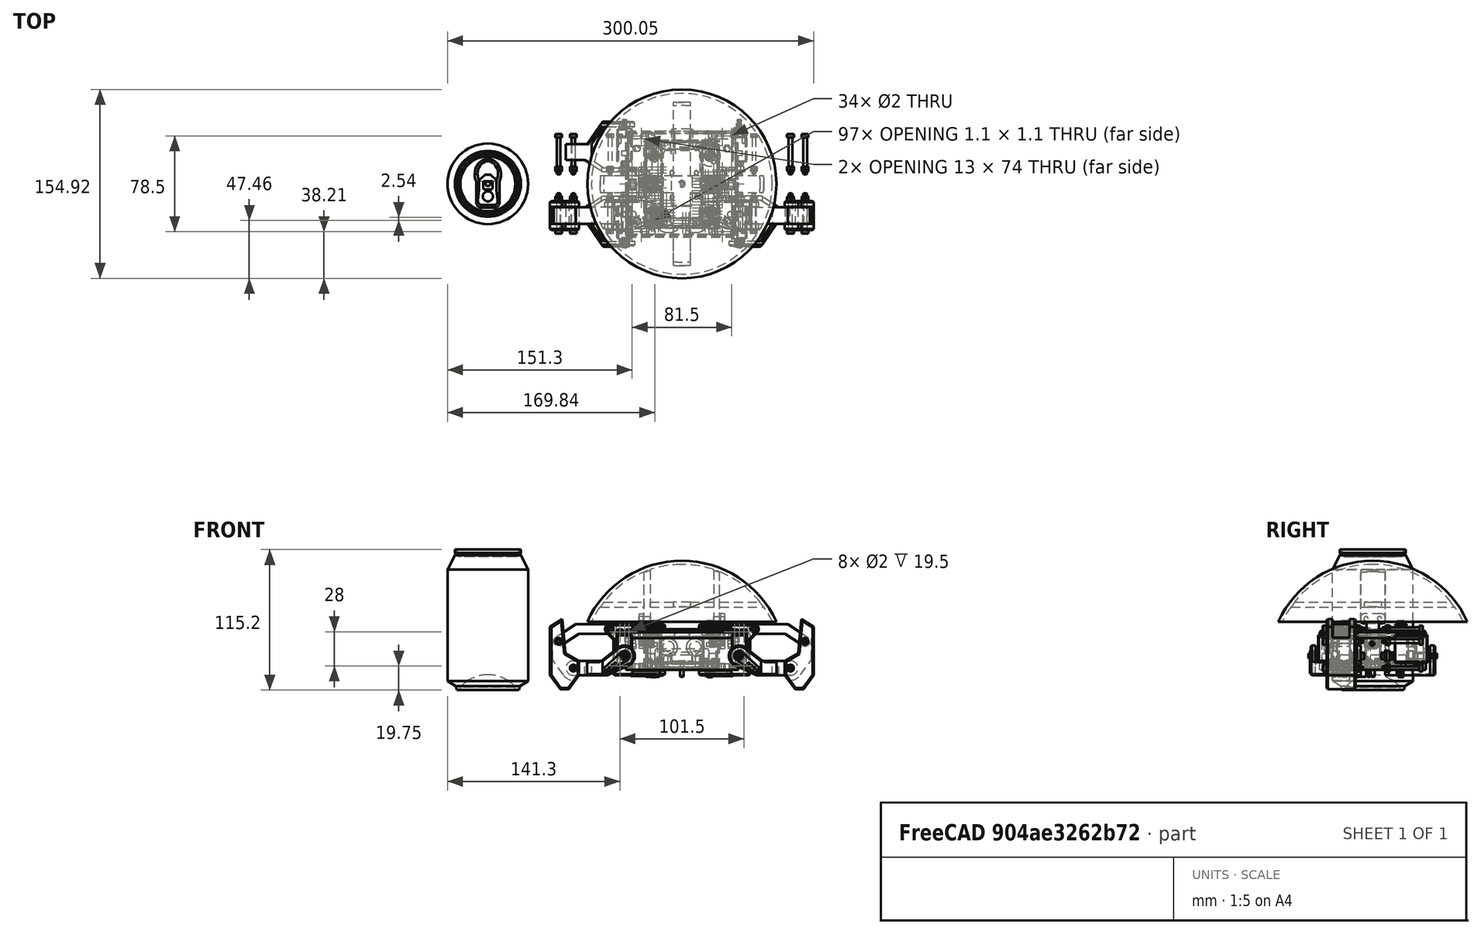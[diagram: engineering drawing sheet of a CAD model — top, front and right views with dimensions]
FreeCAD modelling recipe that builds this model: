
FCSTD DOCUMENT  (FreeCAD 0.16R6692 (Git))
Label: icezumKame
License: All rights reserved
LicenseURL: http://es.wikipedia.org/wiki/Todos_los_derechos_reservados
objects: Part::FeaturePython×116, Part::Cut×39, Part::MultiFuse×32, Sketcher::SketchObject×30, PartDesign::Pad×30, Part::Mirroring×30, Part::Feature×25, Part::Cylinder×23, Part::Box×19, App::DocumentObjectGroup×14, Part::Fillet×10, Part::Chamfer×10, Part::Prism×8, Part::MultiCommon×2, Part::Cone×2, Part::Sphere×2, Spreadsheet::Sheet×1, Mesh::Feature×1
note: 408 computed .brp shape members not serialized (recipe doc carries the construction recipe); baked Part::Feature solids carry a one-line shape summary decoded from their .brp

FEATURE [Part::Feature] Solid001  label="TGY-306G"
  shape: bbox 12.2 x 32 x 31.85 mm, 251 faces (baked)
FEATURE [Part::Box] Box  label="Cubo"
  Height = 10
  Length = 30
  Width = 55
FEATURE [Part::Fillet] Fillet  label="battery"
  Base = -> Box
  Edges = 12 edges r=2.5: [Edge1,Edge2,Edge3,Edge4,Edge5,Edge6,Edge7,Edge8,Edge9,Edge10,Edge11,Edge12]
FEATURE [Part::FeaturePython] Clone002  label="Clone of battery"  # Draft clone (typed FeaturePython)
  Objects = -> [Fillet]
  Placement = pos=(-15,-27.5,-2) rot=(0,0,1;0rad)
  Scale = (1,1,1)
FEATURE [Part::FeaturePython] Clone005  label="Clone of TGY-306G003"  # Draft clone (typed FeaturePython)
  Objects = -> [Solid001]
  Placement = pos=(-23,23,23.3) rot=(0,1,0;3.14159rad)
  Scale = (1,1,1)
FEATURE [Part::Box] Box001  label="main_cube"
  Height = 26
  Length = 92
  Placement = pos=(-46,-43,-3.5) rot=(0,0,1;0rad)
  Width = 87
FEATURE [Part::Feature] Part__Feature  label="final-can"
  Placement = pos=(-159,0,-21) rot=(0,0,1;0rad)
  shape: bbox 66.1 x 66.1 x 115.2 mm, 53 faces (baked)
FEATURE [Sketcher::SketchObject] Sketch  label="servo_sketch"
  Placement = pos=(0,0,-10) rot=(1,0,0;3.14159rad)
  sketch-geometry (14):
    g0: LineSegment StartX=-29.5 StartY=29 StartZ=0 EndX=-16.5 EndY=29 EndZ=0
    g1: LineSegment StartX=-16.5 StartY=29 StartZ=0 EndX=-16.5 EndY=5.5 EndZ=0
    g2: LineSegment StartX=-16.5 StartY=5.5 StartZ=0 EndX=-29.5 EndY=5.5 EndZ=0
    g3: LineSegment StartX=-29.5 StartY=5.5 StartZ=0 EndX=-29.5 EndY=29 EndZ=0
    g4: Circle CenterX=-26.75 CenterY=31.25 CenterZ=0 NormalX=0 NormalY=0 NormalZ=1 Radius=1
    g5: Circle CenterX=-19.25 CenterY=31.25 CenterZ=0 NormalX=0 NormalY=0 NormalZ=1 Radius=1
    g6: Circle CenterX=-26.75 CenterY=3.25 CenterZ=0 NormalX=0 NormalY=0 NormalZ=1 Radius=1
    g7: Circle CenterX=-19.25 CenterY=3.25 CenterZ=0 NormalX=0 NormalY=0 NormalZ=1 Radius=1
    g8: LineSegment [constr] StartX=-29.5 StartY=29 StartZ=0 EndX=-26.75 EndY=31.25 EndZ=0
    g9: LineSegment [constr] StartX=-26.75 StartY=31.25 StartZ=0 EndX=-19.25 EndY=31.25 EndZ=0
    g10: LineSegment [constr] StartX=-19.25 StartY=31.25 StartZ=0 EndX=-16.5 EndY=29 EndZ=0
    g11: LineSegment [constr] StartX=-29.5 StartY=5.5 StartZ=0 EndX=-26.75 EndY=3.25 EndZ=0
    g12: LineSegment [constr] StartX=-26.75 StartY=3.25 StartZ=0 EndX=-19.25 EndY=3.25 EndZ=0
    g13: LineSegment [constr] StartX=-19.25 StartY=3.25 StartZ=0 EndX=-16.5 EndY=5.5 EndZ=0
  constraints (33):
    c: Coincident(g0,g1)
    c: Coincident(g1,g2)
    c: Coincident(g2,g3)
    c: Coincident(g3,g0)
    c: Horizontal(g0)
    c: Horizontal(g2)
    c: Vertical(g1)
    c: Vertical(g3)
    c: Coincident(g0,g8)
    c: Coincident(g8,g4)
    c: Coincident(g8,g9)
    c: Coincident(g9,g5)
    c: Horizontal(g9)
    c: Coincident(g9,g10)
    c: Coincident(g10,g0)
    c: Coincident(g2,g11)
    c: Coincident(g11,g6)
    c: Coincident(g11,g12)
    c: Coincident(g12,g7)
    c: Horizontal(g12)
    c: Coincident(g12,g13)
    c: Coincident(g13,g1)
    c: Radius(g4) = 1
    c: Equal(g4,g5)
    c: Equal(g4,g6)
    c: Equal(g4,g7)
    c: Equal(g8,g10)
    c: Equal(g11,g13)
    c: Distance(g3) = 23.5
    c: Distance(g2) = 13
    c: DistanceY(g-1,g1) = 5.5
    c: DistanceX(g-1,g1) = -16.5
    c: DistanceY(g7,g1) = 2.25
FEATURE [PartDesign::Pad] Pad  label="original_servo_hole"
  Length = 40
  Length2 = 100
  Placement = pos=(0,0,-10) rot=(1,0,0;3.14159rad)
  Reversed = true
  Sketch = -> Sketch
  Type = 0
FEATURE [Part::Box] Box007  label="difference_cube"
  Height = 27
  Length = 88
  Placement = pos=(-44,-41,1.5) rot=(0,0,1;0rad)
  Width = 83
FEATURE [Part::Box] Box008  label="difference_cube_board_bed"
  Height = 27
  Length = 58
  Placement = pos=(-29,-35.5,-2) rot=(0,0,1;0rad)
  Width = 72
FEATURE [Part::Cylinder] Cylinder004  label="Cilindro004"
  Angle = 360
  Height = 50
  Placement = pos=(-23,23,-15) rot=(0,0,1;0rad)
  Radius = 1.75
FEATURE [Part::Cylinder] Cylinder005  label="Cilindro005"
  Angle = 360
  Height = 50
  Placement = pos=(23,23,-15) rot=(0,0,1;0rad)
  Radius = 1.75
FEATURE [Part::Cylinder] Cylinder006  label="Cilindro006"
  Angle = 360
  Height = 50
  Placement = pos=(-23,-23,-15) rot=(0,0,1;0rad)
  Radius = 1.75
FEATURE [Part::Cylinder] Cylinder007  label="Cilindro007"
  Angle = 360
  Height = 50
  Placement = pos=(23,-23,-15) rot=(0,0,1;0rad)
  Radius = 1.75
FEATURE [Part::Box] Box009  label="Cubo009"
  Height = 6
  Length = 62
  Placement = pos=(-31,-36,23) rot=(0,0,1;0rad)
  Width = 72
FEATURE [Part::Chamfer] Chamfer001
  Base = -> Box009
  Edges = 8 edges r=1: [Edge1,Edge2,Edge3,Edge5,Edge6,Edge7,Edge10,Edge12]
FEATURE [Part::MultiFuse] Fusion002
  Shapes = -> [Cylinder004,Cylinder005,Cylinder007,Cylinder006]
FEATURE [Sketcher::SketchObject] Sketch001
  Placement = pos=(0,0,23) rot=(1,0,0;3.14159rad)
  sketch-geometry (4):
    g0: LineSegment StartX=-29 StartY=34 StartZ=0 EndX=29 EndY=34 EndZ=0
    g1: LineSegment StartX=29 StartY=34 StartZ=0 EndX=29 EndY=-34 EndZ=0
    g2: LineSegment StartX=29 StartY=-34 StartZ=0 EndX=-29 EndY=-34 EndZ=0
    g3: LineSegment StartX=-29 StartY=-34 StartZ=0 EndX=-29 EndY=34 EndZ=0
  constraints (12):
    c: Coincident(g0,g1)
    c: Coincident(g1,g2)
    c: Coincident(g2,g3)
    c: Coincident(g3,g0)
    c: Horizontal(g0)
    c: Horizontal(g2)
    c: Vertical(g1)
    c: Vertical(g3)
    c: Symmetric(g2,g1,g-2)
    c: Symmetric(g0,g2,g-1)
    c: Distance(g3) = 68
    c: Distance(g2) = 58
FEATURE [PartDesign::Pad] Pad001
  Length = 2
  Length2 = 100
  Placement = pos=(0,0,23) rot=(1,0,0;3.14159rad)
  Reversed = true
  Sketch = -> Sketch001
  Type = 0
FEATURE [Sketcher::SketchObject] Sketch002
  Placement = pos=(0,0,23) rot=(1,0,0;3.14159rad)
  sketch-geometry (4):
    g0: LineSegment StartX=-16.5 StartY=34 StartZ=0 EndX=16.5 EndY=34 EndZ=0
    g1: LineSegment StartX=16.5 StartY=34 StartZ=0 EndX=16.5 EndY=-34 EndZ=0
    g2: LineSegment StartX=16.5 StartY=-34 StartZ=0 EndX=-16.5 EndY=-34 EndZ=0
    g3: LineSegment StartX=-16.5 StartY=-34 StartZ=0 EndX=-16.5 EndY=34 EndZ=0
  constraints (12):
    c: Coincident(g0,g1)
    c: Coincident(g1,g2)
    c: Coincident(g2,g3)
    c: Coincident(g3,g0)
    c: Horizontal(g0)
    c: Horizontal(g2)
    c: Vertical(g1)
    c: Vertical(g3)
    c: Symmetric(g2,g1,g-2)
    c: Symmetric(g0,g2,g-1)
    c: Distance(g3) = 68
    c: Distance(g2) = 33
FEATURE [PartDesign::Pad] Pad002
  Length = 6
  Length2 = 100
  Placement = pos=(0,0,23) rot=(1,0,0;3.14159rad)
  Reversed = true
  Sketch = -> Sketch002
  Type = 0
FEATURE [Part::MultiFuse] Fusion003
  Placement = pos=(0,0,-1) rot=(0,0,1;0rad)
  Shapes = -> [Pad002,Pad001]
FEATURE [Part::Cut] Cut004
  Base = -> Chamfer001
  Tool = -> Fusion003
FEATURE [Part::Prism] Prism004  label="Prisma004"
  Circumradius = 3.1
  Height = 10
  Placement = pos=(-23,23,0) rot=(0,0,1;0rad)
  Polygon = 6
FEATURE [Part::Prism] Prism005  label="Prisma005"
  Circumradius = 3.1
  Height = 10
  Placement = pos=(23,23,0) rot=(0,0,1;0rad)
  Polygon = 6
FEATURE [Part::Prism] Prism006  label="Prisma006"
  Circumradius = 3.1
  Height = 10
  Placement = pos=(-23,-23,0) rot=(0,0,1;0rad)
  Polygon = 6
FEATURE [Part::Prism] Prism007  label="Prisma007"
  Circumradius = 3.1
  Height = 10
  Placement = pos=(23,-23,0) rot=(0,0,1;0rad)
  Polygon = 6
FEATURE [Part::MultiFuse] Fusion004
  Placement = pos=(0,0,17) rot=(0,0,1;0rad)
  Shapes = -> [Prism007,Prism004,Prism005,Prism006]
FEATURE [Part::Cut] Cut005
  Base = -> Cut004
  Tool = -> Fusion004
FEATURE [Part::Cut] Cut006  label="bod"
  Base = -> Cut005
  Tool = -> Fusion002
FEATURE [Part::FeaturePython] Clone  label="Clone of TGY-306G"  # Draft clone (typed FeaturePython)
  Objects = -> [Solid001]
  Placement = pos=(47,-18,7) rot=(0,-0.707107,0.707107;3.14159rad)
  Scale = (1,1,1)
FEATURE [Part::Cylinder] Cylinder012  label="Cilindro012"
  Angle = 360
  Height = 11
  Placement = pos=(-47,23,7) rot=(1,0,0;1.5708rad)
  Radius = 1.75
FEATURE [Sketcher::SketchObject] Sketch003
  Placement = pos=(0,0,-9) rot=(0,0,1;0rad)
  sketch-geometry (5):
    g0: ArcOfCircle CenterX=-23 CenterY=23 CenterZ=0 NormalX=0 NormalY=0 NormalZ=1 Radius=9 StartAngle=4.71239 EndAngle=7.5465
    g1: LineSegment StartX=-23 StartY=14 StartZ=0 EndX=-56 EndY=14 EndZ=0
    g2: LineSegment StartX=-56 StartY=14 StartZ=0 EndX=-56 EndY=38 EndZ=0
    g3: LineSegment StartX=-56 StartY=38 StartZ=0 EndX=-40.5 EndY=38 EndZ=0
    g4: LineSegment StartX=-40.5 StartY=38 StartZ=0 EndX=-20.2761 EndY=31.5779 EndZ=0
  constraints (16):
    c: Horizontal(g1)
    c: Coincident(g1,g2)
    c: Vertical(g2)
    c: Coincident(g2,g3)
    c: Horizontal(g3)
    c: Coincident(g3,g4)
    c: Coincident(g4,g0)
    c: Coincident(g0,g1)
    c: Tangent(g1,g0)
    c: Tangent(g4,g0)
    c: Radius(g0) = 9
    c: DistanceX(g-1,g0) = -23
    c: DistanceY(g-1,g0) = 23
    c: Distance(g1) = 33
    c: Distance(g2) = 24
    c: Distance(g3) = 15.5
FEATURE [PartDesign::Pad] Pad003
  Length = 42
  Length2 = 100
  Placement = pos=(0,0,-9) rot=(0,0,1;0rad)
  Sketch = -> Sketch003
  Type = 0
FEATURE [Part::Box] Box010  label="Cubo010"
  Height = 35
  Length = 35
  Placement = pos=(-41,0,-5) rot=(0,0,1;0rad)
  Width = 60
FEATURE [Part::Cut] Cut007
  Base = -> Pad003
  Tool = -> Box010
FEATURE [Sketcher::SketchObject] Sketch004
  Placement = pos=(0,14,0) rot=(0,0.707107,0.707107;3.14159rad)
  sketch-geometry (4):
    g0: ArcOfCircle CenterX=59 CenterY=29 CenterZ=0 NormalX=0 NormalY=0 NormalZ=1 Radius=4 StartAngle=5.49779 EndAngle=7.85398
    g1: LineSegment StartX=59 StartY=33 StartZ=0 EndX=54 EndY=33 EndZ=0
    g2: LineSegment StartX=54 StartY=33 StartZ=0 EndX=54 EndY=18.3431 EndZ=0
    g3: LineSegment StartX=54 StartY=18.3431 StartZ=0 EndX=61.8284 EndY=26.1716 EndZ=0
  constraints (12):
    c: Tangent(g0,g1) = -1.5708
    c: Coincident(g1,g2)
    c: Vertical(g2)
    c: Coincident(g2,g3)
    c: Coincident(g3,g0)
    c: Tangent(g0,g3)
    c: Horizontal(g1)
    c: Radius(g0) = 4
    c: Angle(g3,g2) = 0.785398
    c: DistanceY(g-1,g1) = 33
    c: DistanceX(g-1,g1) = 54
    c: Distance(g1) = 5
FEATURE [Part::Cylinder] Cylinder013  label="Cilindro013"
  Angle = 360
  Height = 14
  Placement = pos=(-59,19,29) rot=(-1,0,0;1.5708rad)
  Radius = 5.5
FEATURE [Part::Cut] Cut008
  Base = -> Cut007
  Tool = -> Cylinder013
FEATURE [PartDesign::Pad] Pad004
  Length = 5
  Length2 = 100
  Placement = pos=(0,14,0) rot=(0,0.707107,0.707107;3.14159rad)
  Sketch = -> Sketch004
  Type = 0
FEATURE [Part::FeaturePython] Clone006  label="Clone of Pad004"  # Draft clone (typed FeaturePython)
  Objects = -> [Pad004]
  Placement = pos=(0,33,0) rot=(0,0.707107,0.707107;3.14159rad)
  Scale = (1,1,1)
FEATURE [Part::MultiFuse] Fusion006
  Shapes = -> [Clone006,Pad004]
FEATURE [Part::Cylinder] Cylinder014  label="Cilindro014"
  Angle = 360
  Height = 36
  Placement = pos=(-59,8,29) rot=(-1,0,0;1.5708rad)
  Radius = 1.75
FEATURE [Part::Fillet] Fillet002
  Base = -> Cut008
  Edges = 2 edges r=0.5: [Edge26,Edge33]
FEATURE [Part::Chamfer] Chamfer002
  Base = -> Fusion006
  Edges = 2 edges r=1: [Edge3,Edge16]
FEATURE [Part::Chamfer] Chamfer003
  Base = -> Fillet002
  Edges = 7 edges r=1: [Edge6,Edge8,Edge10,Edge21,Edge23,Edge25,Edge37]
FEATURE [Part::Cut] Cut010
  Base = -> Chamfer003
  Tool = -> Cylinder012
FEATURE [Part::MultiFuse] Fusion007
  Shapes = -> [Cut010,Chamfer002]
FEATURE [Part::Cut] Cut011
  Base = -> Fusion007
  Tool = -> Cylinder014
FEATURE [Part::Cylinder] Cylinder016
  Angle = 360
  Height = 10
  Radius = 5.25
FEATURE [Part::Cylinder] Cylinder017
  Angle = 360
  Height = 10
  Placement = pos=(0,0,-5) rot=(0,0,1;0rad)
  Radius = 4.25
FEATURE [Part::MultiFuse] Fusion008
  Placement = pos=(-23,23,32) rot=(0,0,1;0rad)
  Shapes = -> [Cylinder016,Cylinder017]
FEATURE [Part::Cut] Cut012
  Base = -> Cut011
  Tool = -> Fusion008
FEATURE [Sketcher::SketchObject] Sketch005
  Placement = pos=(0,55,0) rot=(0,0.707107,0.707107;3.14159rad)
  sketch-geometry (8):
    g0: ArcOfCircle CenterX=47 CenterY=7 CenterZ=0 NormalX=0 NormalY=0 NormalZ=1 Radius=8.5 StartAngle=0.910189 EndAngle=4.27175
    g1: LineSegment StartX=52.2156 StartY=13.7118 StartZ=0 EndX=66.0002 EndY=3 EndZ=0
    g2: LineSegment StartX=66.0002 StartY=3 StartZ=0 EndX=89 EndY=3 EndZ=0
    g3: LineSegment StartX=43.3746 StartY=-0.688059 StartZ=0 EndX=61.0008 EndY=-9 EndZ=0
    g4: LineSegment StartX=61.0008 StartY=-9 StartZ=0 EndX=89 EndY=-9 EndZ=0
    g5: ArcOfCircle CenterX=89 CenterY=-3 CenterZ=0 NormalX=0 NormalY=0 NormalZ=1 Radius=6 StartAngle=4.71239 EndAngle=7.85398
    g6: Circle CenterX=47 CenterY=7 CenterZ=0 NormalX=0 NormalY=0 NormalZ=1 Radius=1.7
    g7: Circle CenterX=89 CenterY=-3 CenterZ=0 NormalX=0 NormalY=0 NormalZ=1 Radius=1.7
  constraints (22):
    c: Tangent(g0,g1) = 1.5708
    c: Coincident(g1,g2)
    c: Horizontal(g2)
    c: Tangent(g0,g3) = -1.5708
    c: Coincident(g3,g4)
    c: Horizontal(g4)
    c: Coincident(g5,g2)
    c: Coincident(g5,g4)
    c: DistanceY(g-1,g0) = 7
    c: DistanceX(g-1,g0) = 47
    c: Tangent(g5,g2)
    c: Tangent(g4,g5)
    c: Radius(g0) = 8.5
    c: Radius(g5) = 6
    c: Coincident(g6,g0)
    c: Coincident(g7,g5)
    c: Radius(g7) = 1.7
    c: Equal(g7,g6)
    c: DistanceX(g0,g5) = 42  'x_length'
    c: Angle(g2,g1) = 2.48099
    c: Angle(g4,g3) = 2.70095
    c: DistanceY(g0,g5) = -10  'z_length'
FEATURE [PartDesign::Pad] Pad005
  Length = 50
  Length2 = 100
  Placement = pos=(0,55,0) rot=(0,0.707107,0.707107;3.14159rad)
  Reversed = true
  Sketch = -> Sketch005
  Type = 0
FEATURE [Sketcher::SketchObject] Sketch006
  Placement = pos=(0,0,-20) rot=(0,0,1;0rad)
  sketch-geometry (20):
    g0: LineSegment StartX=-102.641 StartY=32.5 StartZ=0 EndX=-77.6414 EndY=32.5 EndZ=0
    g1: LineSegment StartX=-77.6414 StartY=32.5 StartZ=0 EndX=-65 EndY=51 EndZ=0
    g2: LineSegment StartX=-65 StartY=51 StartZ=0 EndX=-36 EndY=51 EndZ=0
    g3: LineSegment StartX=-36 StartY=10 StartZ=0 EndX=-65 EndY=10 EndZ=0
    g4: LineSegment StartX=-65 StartY=10 StartZ=0 EndX=-79.4811 EndY=19.5 EndZ=0
    g5: LineSegment StartX=-79.4811 StartY=19.5 StartZ=0 EndX=-102.641 EndY=19.5 EndZ=0
    g6: LineSegment StartX=-102.641 StartY=19.5 StartZ=0 EndX=-102.641 EndY=32.5 EndZ=0
    g7: LineSegment StartX=-36 StartY=51 StartZ=0 EndX=-36 EndY=47 EndZ=0
    g8: LineSegment StartX=-36 StartY=47 StartZ=0 EndX=-64.0919 EndY=47 EndZ=0
    g9: LineSegment StartX=-64.0919 StartY=47 StartZ=0 EndX=-74 EndY=32.5 EndZ=0
    g10: LineSegment StartX=-74 StartY=32.5 StartZ=0 EndX=-74 EndY=19.5 EndZ=0
    g11: LineSegment StartX=-74 StartY=19.5 StartZ=0 EndX=-64.0919 EndY=13 EndZ=0
    g12: LineSegment StartX=-64.0919 StartY=13 StartZ=0 EndX=-36 EndY=13 EndZ=0
    g13: LineSegment StartX=-36 StartY=13 StartZ=0 EndX=-36 EndY=10 EndZ=0
    g14: LineSegment [constr] StartX=-79.4811 StartY=19.5 StartZ=0 EndX=-74 EndY=19.5 EndZ=0
    g15: LineSegment [constr] StartX=-77.6414 StartY=32.5 StartZ=0 EndX=-74 EndY=32.5 EndZ=0
    g16: LineSegment [constr] StartX=-64.0919 StartY=47 StartZ=0 EndX=-64.0919 EndY=13 EndZ=0
    g17: LineSegment [constr] StartX=-64.0919 StartY=47 StartZ=0 EndX=-66.5742 EndY=48.6962 EndZ=0
    g18: LineSegment [constr] StartX=-36 StartY=47 StartZ=0 EndX=-36 EndY=13 EndZ=0
    g19: LineSegment [constr] StartX=-64.0919 StartY=13 StartZ=0 EndX=-65.741 EndY=10.4861 EndZ=0
  constraints (56):
    c: Horizontal(g0)
    c: Coincident(g0,g1)
    c: Coincident(g1,g2)
    c: Horizontal(g2)
    c: Horizontal(g3)
    c: Coincident(g3,g4)
    c: Coincident(g4,g5)
    c: Horizontal(g5)
    c: Coincident(g5,g6)
    c: Coincident(g6,g0)
    c: Vertical(g6)
    c: Distance(g6) = 13
    c: Coincident(g2,g7)
    c: Vertical(g7)
    c: Coincident(g7,g8)
    c: Horizontal(g8)
    c: Coincident(g8,g9)
    c: Coincident(g9,g10)
    c: Vertical(g10)
    c: Coincident(g10,g11)
    c: Coincident(g11,g12)
    c: Horizontal(g12)
    c: Coincident(g12,g13)
    c: Coincident(g13,g3)
    c: Vertical(g13)
    c: Distance(g13) = 3
    c: Coincident(g14,g4)
    c: Horizontal(g14)
    c: Coincident(g15,g0)
    c: Coincident(g15,g9)
    c: Horizontal(g15)
    c: Coincident(g16,g8)
    c: Coincident(g16,g11)
    c: Vertical(g16)
    c: Parallel(g9,g1)
    c: Parallel(g4,g11)
    c: Coincident(g17,g8)
    c: PointOnObject(g17,g1)
    c: Perpendicular(g1,g17)
    c: Coincident(g14,g10)
    c: Distance(g7) = 4
    c: Coincident(g18,g12)
    c: Vertical(g18)
    c: Coincident(g7,g18)
    c: Distance(g18) = 34
    c: DistanceY(g5,g3) = -9.5
    c: DistanceX(g-1,g3) = -36
    c: Distance(g3) = 29
    c: Equal(g2,g3)
    c: Coincident(g19,g11)
    c: PointOnObject(g19,g4)
    c: Equal(g19,g17)
    c: Perpendicular(g4,g19)
    c: DistanceY(g-1,g12) = 13
    c: Distance(g0) = 25
    c: DistanceX(g10,g3) = 9
FEATURE [PartDesign::Pad] Pad006
  Length = 40
  Length2 = 100
  Placement = pos=(0,0,-20) rot=(0,0,1;0rad)
  Sketch = -> Sketch006
  Type = 0
FEATURE [Sketcher::SketchObject] Sketch007
  Placement = pos=(0,19.25,0) rot=(0,0.707107,0.707107;3.14159rad)
  sketch-geometry (8):
    g0: ArcOfCircle CenterX=59 CenterY=29 CenterZ=0 NormalX=0 NormalY=0 NormalZ=1 Radius=4 StartAngle=1.5708 EndAngle=4.71239
    g1: LineSegment StartX=59 StartY=33 StartZ=0 EndX=86.7994 EndY=33 EndZ=0
    g2: LineSegment StartX=86.7994 StartY=33 StartZ=0 EndX=103.18 EndY=22.3539 EndZ=0
    g3: LineSegment StartX=59 StartY=25 StartZ=0 EndX=84.428 EndY=25 EndZ=0
    g4: LineSegment StartX=84.428 StartY=25 StartZ=0 EndX=98.8202 EndY=15.6461 EndZ=0
    g5: ArcOfCircle CenterX=101 CenterY=19 CenterZ=0 NormalX=0 NormalY=0 NormalZ=1 Radius=4 StartAngle=4.13607 EndAngle=7.27765
    g6: Circle CenterX=59 CenterY=29 CenterZ=0 NormalX=0 NormalY=0 NormalZ=1 Radius=1.7
    g7: Circle CenterX=101 CenterY=19 CenterZ=0 NormalX=0 NormalY=0 NormalZ=1 Radius=1.7
  constraints (22):
    c: Tangent(g0,g1) = 1.5708
    c: Coincident(g1,g2)
    c: Tangent(g0,g3) = -1.5708
    c: Coincident(g3,g4)
    c: Coincident(g5,g2)
    c: Coincident(g5,g4)
    c: Tangent(g2,g5)
    c: Tangent(g4,g5)
    c: Parallel(g1,g3)
    c: Parallel(g2,g4)
    c: Horizontal(g1)
    c: Radius(g0) = 4
    c: Equal(g0,g5)
    c: Coincident(g6,g0)
    c: Coincident(g7,g5)
    c: Radius(g6) = 1.7
    c: Equal(g6,g7)
    c: DistanceY(g-1,g0) = 29
    c: DistanceX(g-1,g0) = 59
    c: Angle(g1,g2) = 2.56527
    c: DistanceY(g0,g5) = -10  'z_length'
    c: DistanceX(g0,g5) = 42  'x_legth'
FEATURE [PartDesign::Pad] Pad007  label="legA"
  Length = 13.5
  Length2 = 100
  Placement = pos=(0,19.25,0) rot=(0,0.707107,0.707107;3.14159rad)
  Sketch = -> Sketch007
  Type = 0
FEATURE [Sketcher::SketchObject] Sketch008
  Placement = pos=(0,14,0) rot=(0,0.707107,0.707107;3.14159rad)
  sketch-geometry (14):
    g0: LineSegment StartX=84.3518 StartY=2.97051 StartZ=0 EndX=95.4438 EndY=9.10709 EndZ=0
    g1: LineSegment StartX=95.4438 StartY=9.10709 StartZ=0 EndX=97.9681 EndY=37.1902 EndZ=0
    g2: LineSegment StartX=97.9681 StartY=37.1902 StartZ=0 EndX=108 EndY=30.9216 EndZ=0
    g3: LineSegment StartX=108 StartY=30.9216 StartZ=0 EndX=108 EndY=-9 EndZ=0
    g4: LineSegment StartX=108 StartY=-9 StartZ=0 EndX=99.6759 EndY=-20.4078 EndZ=0
    g5: LineSegment StartX=99.6759 StartY=-20.4078 StartZ=0 EndX=92.6759 EndY=-20.4078 EndZ=0
    g6: LineSegment StartX=92.6759 StartY=-20.4078 StartZ=0 EndX=84.3518 EndY=-9 EndZ=0
    g7: LineSegment StartX=84.3518 StartY=2.97051 StartZ=0 EndX=84.3518 EndY=-9 EndZ=0
    g8: Circle [constr] CenterX=96.1759 CenterY=-9.11307 CenterZ=0 NormalX=0 NormalY=0 NormalZ=1 Radius=11.8246
    g9: LineSegment [constr] StartX=84.3518 StartY=-9 StartZ=0 EndX=108 EndY=-9 EndZ=0
    g10: Circle CenterX=101 CenterY=19 CenterZ=0 NormalX=0 NormalY=0 NormalZ=1 Radius=1.7
    g11: Circle CenterX=89 CenterY=-3 CenterZ=0 NormalX=0 NormalY=0 NormalZ=1 Radius=1.7
    g12: LineSegment [constr] StartX=89 StartY=-3 StartZ=0 EndX=84.3518 EndY=-3 EndZ=0
    g13: LineSegment [constr] StartX=96.3705 StartY=19.4161 StartZ=0 EndX=101 EndY=19 EndZ=0
  constraints (35):
    c: Coincident(g1,g2)
    c: Coincident(g2,g3)
    c: Coincident(g3,g4)
    c: Coincident(g4,g5)
    c: Horizontal(g5)
    c: Coincident(g5,g6)
    c: Coincident(g7,g0)
    c: Coincident(g7,g6)
    c: Vertical(g7)
    c: Coincident(g0,g1)
    c: PointOnObject(g6,g8)
    c: PointOnObject(g5,g8)
    c: PointOnObject(g4,g8)
    c: PointOnObject(g3,g8)
    c: Coincident(g9,g6)
    c: Coincident(g9,g3)
    c: Horizontal(g9)
    c: Vertical(g3)
    c: DistanceY(g-1,g6) = -9
    c: DistanceX(g11,g10) = 12
    c: DistanceY(g11,g10) = 22
    c: Coincident(g12,g11)
    c: PointOnObject(g12,g7)
    c: Perpendicular(g7,g12)
    c: PointOnObject(g13,g1)
    c: Coincident(g13,g10)
    c: Perpendicular(g1,g13)
    c: Equal(g13,g12)
    c: Radius(g10) = 1.7
    c: Equal(g10,g11)
    c: DistanceX(g11,g3) = 19
    c: DistanceY(g6,g11) = 6
    c: Distance(g5) = 7
    c: DistanceX(g-1,g11) = 89
    c: Angle(g2,g3) = 2.1293
FEATURE [PartDesign::Pad] Pad008
  Length = 24
  Length2 = 100
  Placement = pos=(0,14,0) rot=(0,0.707107,0.707107;3.14159rad)
  Sketch = -> Sketch008
  Type = 0
FEATURE [Part::MultiCommon] Common  label="pre-bracket"
  Shapes = -> [Pad006,Pad005]
FEATURE [Part::Chamfer] Chamfer004
  Base = -> Common
  Edges = 5 edges r=1: [Edge6,Edge9,Edge20,Edge33,Edge34]
FEATURE [Part::MultiFuse] Fusion009
  Placement = pos=(-47,11,7) rot=(1,0,0;1.5708rad)
  Shapes = -> [Cylinder016,Cylinder017]
FEATURE [Part::Cut] Cut013
  Base = -> Chamfer004
  Tool = -> Fusion009
FEATURE [Sketcher::SketchObject] Sketch009
  Placement = pos=(0,33,0) rot=(0,0.707107,0.707107;3.14159rad)
  sketch-geometry (8):
    g0: ArcOfCircle CenterX=89 CenterY=-3 CenterZ=0 NormalX=0 NormalY=0 NormalZ=1 Radius=10 StartAngle=4.71239 EndAngle=5.67573
    g1: LineSegment StartX=97.2111 StartY=-8.70777 StartZ=0 EndX=106 EndY=3.93578 EndZ=0
    g2: LineSegment StartX=106 StartY=3.93578 StartZ=0 EndX=106 EndY=22 EndZ=0
    g3: LineSegment StartX=106 StartY=22 StartZ=0 EndX=112.578 EndY=22 EndZ=0
    g4: LineSegment StartX=112.578 StartY=22 StartZ=0 EndX=112.578 EndY=42.6594 EndZ=0
    g5: LineSegment StartX=112.578 StartY=42.6594 StartZ=0 EndX=77.1596 EndY=42.6594 EndZ=0
    g6: LineSegment StartX=77.1596 StartY=42.6594 StartZ=0 EndX=77.1596 EndY=-13 EndZ=0
    g7: LineSegment StartX=77.1596 StartY=-13 StartZ=0 EndX=89 EndY=-13 EndZ=0
  constraints (20):
    c: Tangent(g0,g1) = -1.5708
    c: Coincident(g1,g2)
    c: Vertical(g2)
    c: Coincident(g2,g3)
    c: Horizontal(g3)
    c: Coincident(g3,g4)
    c: Vertical(g4)
    c: Coincident(g4,g5)
    c: Horizontal(g5)
    c: Coincident(g5,g6)
    c: Vertical(g6)
    c: Coincident(g7,g6)
    c: Coincident(g7,g0)
    c: Horizontal(g7)
    c: Tangent(g7,g0)
    c: DistanceX(g-1,g1) = 106
    c: DistanceX(g-1,g0) = 89
    c: Radius(g0) = 10
    c: DistanceY(g-1,g0) = -3
    c: DistanceY(g-1,g2) = 22
FEATURE [PartDesign::Pad] Pad009
  Length = 14
  Length2 = 100
  Placement = pos=(0,33,0) rot=(0,0.707107,0.707107;3.14159rad)
  Reversed = true
  Sketch = -> Sketch009
  Type = 0
FEATURE [Part::Cut] Cut014
  Base = -> Pad008
  Tool = -> Pad009
FEATURE [Part::Chamfer] Chamfer005  label="foot"
  Base = -> Cut014
  Edges = 18 edges r=1: [Edge1,Edge5,Edge6,Edge7,Edge8,Edge9,Edge10,Edge11,Edge30,Edge35,Edge37,Edge38,Edge41,Edge49,Edge53,Edge54,Edge55,Edge56]
FEATURE [Sketcher::SketchObject] Sketch010  label="servo_room"
  Placement = pos=(0,41,0) rot=(0,0.707107,0.707107;3.14159rad)
  expr: Placement.Base.z = fake_axis_nut_room.Placement.Base.z - configuration.servo_D / 2 - 1
  expr: Constraints.length_B = configuration.servo_B + 2 * configuration.tolerance_default
  expr: Constraints.length_D = configuration.servo_D + 2 * configuration.tolerance_default + 0.5
  expr: Placement.Base.y = 59.5 - configuration.servo_F + 2 * configuration.tolerance_default
  sketch-geometry (27):
    g0: LineSegment StartX=40.5 StartY=24.5 StartZ=0 EndX=53.5 EndY=24.5 EndZ=0
    g1: LineSegment StartX=53.5 StartY=24.5 StartZ=0 EndX=53.5 EndY=1 EndZ=0
    g2: LineSegment StartX=53.5 StartY=1 StartZ=0 EndX=40.5 EndY=1 EndZ=0
    g3: LineSegment [constr] StartX=40.5 StartY=1 StartZ=0 EndX=40.5 EndY=24.5 EndZ=0
    g4: Circle CenterX=43.25 CenterY=26.75 CenterZ=0 NormalX=0 NormalY=0 NormalZ=1 Radius=1
    g5: Circle CenterX=50.75 CenterY=26.75 CenterZ=0 NormalX=0 NormalY=0 NormalZ=1 Radius=1
    g6: Circle CenterX=43.25 CenterY=-1.25 CenterZ=0 NormalX=0 NormalY=0 NormalZ=1 Radius=1
    g7: Circle CenterX=50.75 CenterY=-1.25 CenterZ=0 NormalX=0 NormalY=0 NormalZ=1 Radius=1
    g8: LineSegment [constr] StartX=50.75 StartY=26.75 StartZ=0 EndX=50.75 EndY=-1.25 EndZ=0
    g9: LineSegment [constr] StartX=43.25 StartY=-1.25 StartZ=0 EndX=43.25 EndY=26.75 EndZ=0
    g10: LineSegment [constr] StartX=40.5 StartY=24.5 StartZ=0 EndX=43.25 EndY=26.75 EndZ=0
    g11: LineSegment [constr] StartX=50.75 StartY=26.75 StartZ=0 EndX=53.5 EndY=24.5 EndZ=0
    g12: LineSegment [constr] StartX=40.5 StartY=1 StartZ=0 EndX=43.25 EndY=-1.25 EndZ=0
    g13: LineSegment [constr] StartX=53.5 StartY=1 StartZ=0 EndX=50.75 EndY=-1.25 EndZ=0
    g14: LineSegment [constr] StartX=40.5 StartY=24.5 StartZ=0 EndX=47 EndY=12.75 EndZ=0
    g15: LineSegment [constr] StartX=47 StartY=12.75 StartZ=0 EndX=53.5 EndY=1 EndZ=0
    g16: LineSegment [constr] StartX=47 StartY=12.75 StartZ=0 EndX=53.5 EndY=24.5 EndZ=0
    g17: LineSegment [constr] StartX=47 StartY=12.75 StartZ=0 EndX=40.5 EndY=1 EndZ=0
    g18: LineSegment [constr] StartX=43.25 StartY=26.75 StartZ=0 EndX=47 EndY=26.75 EndZ=0
    g19: LineSegment [constr] StartX=47 StartY=26.75 StartZ=0 EndX=50.75 EndY=26.75 EndZ=0
    g20: LineSegment [constr] StartX=43.25 StartY=-1.25 StartZ=0 EndX=47 EndY=-1.25 EndZ=0
    g21: LineSegment [constr] StartX=47 StartY=-1.25 StartZ=0 EndX=50.75 EndY=-1.25 EndZ=0
    g22: Circle CenterX=47 CenterY=-1.25 CenterZ=0 NormalX=0 NormalY=0 NormalZ=1 Radius=1
    g23: Circle CenterX=47 CenterY=26.75 CenterZ=0 NormalX=0 NormalY=0 NormalZ=1 Radius=1
    g24: LineSegment StartX=40.5 StartY=24.5 StartZ=0 EndX=30.5 EndY=24.5 EndZ=0
    g25: LineSegment StartX=30.5 StartY=24.5 StartZ=0 EndX=30.5 EndY=1 EndZ=0
    g26: LineSegment StartX=30.5 StartY=1 StartZ=0 EndX=40.5 EndY=1 EndZ=0
  constraints (67):
    c: Coincident(g0,g1)
    c: Coincident(g1,g2)
    c: Coincident(g2,g3)
    c: Coincident(g3,g0)
    c: Horizontal(g0)
    c: Horizontal(g2)
    c: Vertical(g1)
    c: Vertical(g8)
    c: Vertical(g9)
    c: Coincident(g8,g7)
    c: Coincident(g10,g0)  'Constraint21'
    c: Coincident(g10,g4)  'Constraint18'
    c: Coincident(g11,g5)  'Constraint15'
    c: Coincident(g11,g0)  'Constraint14'
    c: Coincident(g12,g2)
    c: Coincident(g12,g6)
    c: Coincident(g13,g1)
    c: Coincident(g13,g7)
    c: Radius(g4) = 1
    c: Equal(g4,g5)
    c: Equal(g4,g6)
    c: Equal(g4,g7)
    c: Distance(g2) = 13  'length_D'
    c: Distance(g3) = 23.5  'length_B'
    c: Coincident(g14,g0)  'Constraint44'
    c: Coincident(g15,g14)  'Constraint40'
    c: Coincident(g15,g1)  'Constraint37'
    c: Coincident(g16,g14)  'Constraint35'
    c: Coincident(g16,g0)  'Constraint34'
    c: Coincident(g17,g14)  'Constraint33'
    c: Coincident(g17,g2)  'Constraint32'
    c: Equal(g14,g16)
    c: Equal(g16,g15)
    c: Equal(g15,g17)
    c: DistanceY(g-1,g14) = 12.75  'servo_center'
    c: DistanceX(g-1,g14) = 47
    c: Coincident(g18,g4)
    c: Coincident(g18,g19)
    c: Coincident(g19,g5)
    c: Horizontal(g19)
    c: Coincident(g4,g9)
    c: Coincident(g8,g5)
    c: Coincident(g20,g6)
    c: Horizontal(g20)
    c: Coincident(g20,g21)
    c: Coincident(g21,g7)
    c: Coincident(g22,g20)
    c: Coincident(g23,g18)
    c: Equal(g23,g5)
    c: Equal(g18,g19)
    c: Equal(g20,g21)
    c: Equal(g22,g6)
    c: Coincident(g9,g6)
    c: Horizontal(g21)
    c: Horizontal(g18)
    c: Equal(g10,g11)
    c: Equal(g10,g12)
    c: Distance(g6,g7) = 7.5
    c: DistanceY(g0,g4) = 2.25
    c: Coincident(g0,g24)
    c: Horizontal(g24)
    c: Coincident(g24,g25)
    c: Vertical(g25)
    c: Coincident(g25,g26)
    c: Coincident(g26,g2)
    c: Horizontal(g26)
    c: Distance(g26) = 10
FEATURE [PartDesign::Pad] Pad010
  Length = 22.5
  Length2 = 100
  Placement = pos=(0,41,0) rot=(0,0.707107,0.707107;3.14159rad)
  Reversed = true
  Sketch = -> Sketch010
  Type = 0
FEATURE [Part::Cut] Cut015
  Base = -> Cut012
  Tool = -> Pad010
FEATURE [Sketcher::SketchObject] Sketch011
  Placement = pos=(0,0,-10) rot=(1,0,0;3.14159rad)
  sketch-geometry (4):
    g0: ArcOfCircle CenterX=-48.5 CenterY=-25 CenterZ=0 NormalX=0 NormalY=0 NormalZ=1 Radius=2.2 StartAngle=1.5708 EndAngle=4.71239
    g1: ArcOfCircle CenterX=-39.5 CenterY=-25 CenterZ=0 NormalX=0 NormalY=0 NormalZ=1 Radius=2.2 StartAngle=4.71239 EndAngle=7.85398
    g2: LineSegment StartX=-48.5 StartY=-27.2 StartZ=0 EndX=-39.5 EndY=-27.2 EndZ=0
    g3: LineSegment StartX=-48.5 StartY=-22.8 StartZ=0 EndX=-39.5 EndY=-22.8 EndZ=0
  constraints (10):
    c: Tangent(g0,g3) = 1.5708
    c: Tangent(g0,g2) = -1.5708
    c: Tangent(g2,g1) = -1.5708
    c: Tangent(g3,g1) = 1.5708
    c: Horizontal(g2)
    c: Equal(g0,g1)
    c: Distance(g3) = 9
    c: Radius(g0) = 2.2
    c: DistanceX(g-1,g0) = -48.5
    c: DistanceY(g-1,g0) = -25
FEATURE [PartDesign::Pad] Pad011
  Length = 15
  Length2 = 100
  Placement = pos=(0,0,-10) rot=(1,0,0;3.14159rad)
  Reversed = true
  Sketch = -> Sketch011
  Type = 0
FEATURE [Part::Chamfer] Chamfer006
  Base = -> Cut015
  Edges = 1 edges r=2: [Edge57]
FEATURE [Part::Cut] Cut016
  Base = -> Chamfer006
  Tool = -> Pad011
FEATURE [Part::Chamfer] Chamfer007
  Base = -> Cut016
  Edges = 1 edges r=1: [Edge97]
FEATURE [Part::Prism] Prism008  label="fake_axis_nut_room"
  Circumradius = 3.2
  Height = 10
  Placement = pos=(-47,25.5,7) rot=(1,0,0;1.5708rad)
  Polygon = 6
FEATURE [Part::Cut] Cut017
  Base = -> Chamfer007
  Tool = -> Prism008
FEATURE [Part::Feature] Cut018  label="horn001"
  Placement = pos=(-23,23,-4.5) rot=(0.866025,0.5,0;3.14159rad)
  shape: bbox 22.95 x 16 x 5 mm, 16 faces (baked)
FEATURE [Part::FeaturePython] Clone007  label="Clone of horn001"  # Draft clone (typed FeaturePython)
  Objects = -> [Cut018]
  Placement = pos=(-23,23,-4.5) rot=(0.866025,0.5,0;3.14159rad)
  Scale = (1,1,1)
FEATURE [Part::FeaturePython] Clone008  label="Clone of horn002"  # Draft clone (typed FeaturePython)
  Objects = -> [Cut018]
  Placement = pos=(-47.025,46.5,7.03288) rot=(0.324098,0.66894,0.66894;3.76843rad)
  Scale = (1,1,1)
FEATURE [Sketcher::SketchObject] Sketch012
  Placement = pos=(0,49,0) rot=(0,0.707107,0.707107;3.14159rad)
  sketch-geometry (5):
    g0: ArcOfCircle CenterX=47 CenterY=7 CenterZ=0 NormalX=0 NormalY=0 NormalZ=1 Radius=4.25 StartAngle=0.819815 EndAngle=4.11947
    g1: ArcOfCircle CenterX=61.8696 CenterY=-4.82778 CenterZ=0 NormalX=0 NormalY=0 NormalZ=1 Radius=2.75 StartAngle=4.11947 EndAngle=7.103
    g2: LineSegment StartX=49.9 StartY=10.1068 StartZ=0 EndX=63.746 EndY=-2.81748 EndZ=0
    g3: LineSegment StartX=44.6252 StartY=3.47543 StartZ=0 EndX=60.3329 EndY=-7.10838 EndZ=0
    g4: LineSegment [constr] StartX=47 StartY=7 StartZ=0 EndX=61.8696 EndY=-4.82778 EndZ=0
  constraints (16):
    c: Coincident(g2,g0)
    c: Coincident(g2,g1)
    c: Coincident(g3,g0)
    c: Coincident(g1,g3)
    c: Tangent(g0,g3)
    c: Tangent(g0,g2)
    c: Tangent(g2,g1)
    c: Tangent(g3,g1)
    c: Radius(g0) = 4.25
    c: Radius(g1) = 2.75
    c: Distance(g0,g1) = 19
    c: DistanceY(g-1,g0) = 7
    c: DistanceX(g-1,g0) = 47
    c: Coincident(g4,g0)
    c: Coincident(g4,g1)
    c: Angle(g-1,g4) = 2.46964
FEATURE [PartDesign::Pad] Pad012
  Length = 10
  Length2 = 100
  Placement = pos=(0,49,0) rot=(0,0.707107,0.707107;3.14159rad)
  Sketch = -> Sketch012
  Type = 0
FEATURE [Sketcher::SketchObject] Sketch014
  Placement = pos=(23.25,34,-10) rot=(0,0,1;3.22886rad)
  sketch-geometry (4):
    g0: ArcOfCircle CenterX=47 CenterY=7 CenterZ=0 NormalX=0 NormalY=0 NormalZ=1 Radius=4.25 StartAngle=0.879517 EndAngle=4.17917
    g1: ArcOfCircle CenterX=62.5488 CenterY=-3.91947 CenterZ=0 NormalX=0 NormalY=0 NormalZ=1 Radius=2.75 StartAngle=4.17917 EndAngle=7.1627
    g2: LineSegment StartX=49.7095 StartY=10.2743 StartZ=0 EndX=64.302 EndY=-1.80079 EndZ=0
    g3: LineSegment StartX=44.8397 StartY=3.34 StartZ=0 EndX=61.151 EndY=-6.2877 EndZ=0
  constraints (13):
    c: Coincident(g2,g0)
    c: Coincident(g2,g1)
    c: Coincident(g3,g0)
    c: Coincident(g1,g3)
    c: Tangent(g0,g3)
    c: Tangent(g0,g2)
    c: Tangent(g2,g1)
    c: Tangent(g3,g1)
    c: Radius(g0) = 4.25
    c: Radius(g1) = 2.75
    c: Distance(g0,g1) = 19
    c: DistanceY(g-1,g0) = 7
    c: DistanceX(g-1,g0) = 47
FEATURE [PartDesign::Pad] Pad014
  Length = 3
  Length2 = 100
  Placement = pos=(23.25,34,-10) rot=(0,0,1;3.22886rad)
  Sketch = -> Sketch014
  Type = 0
FEATURE [Sketcher::SketchObject] Sketch016
  Placement = pos=(23.25,34,-10) rot=(0,0,1;3.22886rad)
  sketch-geometry (5):
    g0: ArcOfCircle [constr] CenterX=47 CenterY=7 CenterZ=0 NormalX=0 NormalY=0 NormalZ=1 Radius=4.25 StartAngle=0.879517 EndAngle=4.17917
    g1: ArcOfCircle [constr] CenterX=62.5488 CenterY=-3.91947 CenterZ=0 NormalX=0 NormalY=0 NormalZ=1 Radius=2.75 StartAngle=4.17917 EndAngle=7.1627
    g2: LineSegment [constr] StartX=49.7095 StartY=10.2743 StartZ=0 EndX=64.302 EndY=-1.80079 EndZ=0
    g3: LineSegment [constr] StartX=44.8397 StartY=3.34 StartZ=0 EndX=61.151 EndY=-6.2877 EndZ=0
    g4: Circle CenterX=47 CenterY=7 CenterZ=0 NormalX=0 NormalY=0 NormalZ=1 Radius=4.25
  constraints (15):
    c: Coincident(g2,g0)
    c: Coincident(g2,g1)
    c: Coincident(g3,g0)
    c: Coincident(g1,g3)
    c: Tangent(g0,g3)
    c: Tangent(g0,g2)
    c: Tangent(g2,g1)
    c: Tangent(g3,g1)
    c: Radius(g0) = 4.25
    c: Radius(g1) = 2.75
    c: Distance(g0,g1) = 19
    c: DistanceY(g-1,g0) = 7
    c: DistanceX(g-1,g0) = 47
    c: Coincident(g4,g0)
    c: Equal(g4,g0)
FEATURE [PartDesign::Pad] Pad015
  Length = 30
  Length2 = 100
  Placement = pos=(23.25,34,-10) rot=(0,0,1;3.22886rad)
  Sketch = -> Sketch016
  Type = 0
FEATURE [Part::MultiFuse] Fusion011
  Shapes = -> [Pad014,Pad015]
FEATURE [Part::Cut] Cut020  label="bracket"
  Base = -> Cut017
  Tool = -> Fusion011
FEATURE [Part::Mirroring] Part__Mirroring006  label="Clone of horn001 (Mirror #7)"
  Base = (0,0,0)
  Normal = (1,0,0)
  Source = -> Clone007
FEATURE [Part::Mirroring] Part__Mirroring007  label="Clone of horn002 (Mirror #8)"
  Base = (0,0,0)
  Normal = (1,0,0)
  Source = -> Clone008
FEATURE [Part::Mirroring] Part__Mirroring008  label="Clone of horn001 (Mirror #9)"
  Base = (0,0,0)
  Normal = (0,1,0)
  Source = -> Clone007
FEATURE [Part::Mirroring] Part__Mirroring009  label="Clone of horn002 (Mirror #10)"
  Base = (0,0,0)
  Normal = (0,1,0)
  Source = -> Clone008
FEATURE [Part::Mirroring] Part__Mirroring010  label="Clone of horn001 (Mirror #11)"
  Base = (0,0,0)
  Normal = (0,1,0)
  Source = -> Part__Mirroring006
FEATURE [Part::Mirroring] Part__Mirroring011  label="Clone of horn002 (Mirror #12)"
  Base = (0,0,0)
  Normal = (0,1,0)
  Source = -> Part__Mirroring007
FEATURE [App::DocumentObjectGroup] Grupo006  label="horns"
  Group = -> [Part__Mirroring008,Part__Mirroring009,Part__Mirroring010,Part__Mirroring011]
FEATURE [Part::FeaturePython] Clone011  label="Clone of legA"  # Draft clone (typed FeaturePython)
  Objects = -> [Pad007]
  Placement = pos=(0,19.25,0) rot=(0,0.707107,0.707107;3.14159rad)
  Scale = (1,1,1)
FEATURE [Part::FeaturePython] Clone012  label="Clone of foot"  # Draft clone (typed FeaturePython)
  Objects = -> [Chamfer005]
  Scale = (1,1,1)
FEATURE [Part::FeaturePython] Clone014  label="Clone of bracket"  # Draft clone (typed FeaturePython)
  Objects = -> [Cut020]
  Scale = (1,1,1)
FEATURE [Part::Mirroring] Part__Mirroring014  label="Clone of legA (Mirror #15)"
  Base = (0,0,0)
  Normal = (1,0,0)
  Source = -> Clone011
FEATURE [Part::Mirroring] Part__Mirroring015  label="Clone of foot (Mirror #16)"
  Base = (0,0,0)
  Normal = (1,0,0)
  Source = -> Clone012
FEATURE [Part::Mirroring] Part__Mirroring017  label="Clone of bracket (Mirror #18)"
  Base = (0,0,0)
  Normal = (1,0,0)
  Source = -> Clone014
FEATURE [Part::Mirroring] Part__Mirroring018  label="Clone of legA (Mirror #17)"
  Base = (0,0,0)
  Normal = (0,1,0)
  Source = -> Clone011
FEATURE [Part::Mirroring] Part__Mirroring019  label="Clone of foot (Mirror #18)"
  Base = (0,0,0)
  Normal = (0,1,0)
  Source = -> Clone012
FEATURE [Part::Mirroring] Part__Mirroring021  label="Clone of bracket (Mirror #20)"
  Base = (0,0,0)
  Normal = (0,1,0)
  Source = -> Clone014
FEATURE [Part::Mirroring] Part__Mirroring022  label="Clone of legA (Mirror #21)"
  Base = (67.9687,3.8147e-06,24.0028)
  Normal = (0,1,-1.19209e-07)
  Source = -> Part__Mirroring014
FEATURE [Part::Mirroring] Part__Mirroring023  label="Clone of foot (Mirror #22)"
  Base = (0,0,0)
  Normal = (0,1,0)
  Source = -> Part__Mirroring015
FEATURE [Part::Mirroring] Part__Mirroring025  label="Clone of bracket (Mirror #24)"
  Base = (0,0,0)
  Normal = (0,1,0)
  Source = -> Part__Mirroring017
FEATURE [Part::Feature] Pad016  label="eye-base"
  Placement = pos=(-11,-36.1,14) rot=(1,0,0;1.5708rad)
  shape: bbox 15 x 0.3 x 15 mm, 3 faces (baked)
FEATURE [Part::Feature] Pad017  label="black-eye"
  Placement = pos=(-11,-36.1,14) rot=(1,0,0;1.5708rad)
  shape: bbox 9.7 x 0.4 x 9.7 mm, 3 faces (baked)
FEATURE [Part::Feature] Fillet004  label="eye-cover"
  Placement = pos=(-11,-36.1,14) rot=(1,0,0;1.5708rad)
  shape: bbox 18.49 x 3.9 x 19.71 mm, 4 faces (baked)
FEATURE [Part::Feature] Pad018  label="eye-base001"
  Placement = pos=(11,-36.1,14) rot=(1,0,0;1.5708rad)
  shape: bbox 15 x 0.3 x 15 mm, 3 faces (baked)
FEATURE [Part::Feature] Pad019  label="black-eye001"
  Placement = pos=(11,-36.1,14) rot=(1,0,0;1.5708rad)
  shape: bbox 9.7 x 0.4 x 9.7 mm, 3 faces (baked)
FEATURE [Part::Feature] Fillet005  label="eye-cover001"
  Placement = pos=(11,-36.1,14) rot=(1,0,0;1.5708rad)
  shape: bbox 18.49 x 3.9 x 19.71 mm, 4 faces (baked)
FEATURE [Sketcher::SketchObject] Sketch017
  Placement = pos=(0,45,0) rot=(0,0.707107,0.707107;3.14159rad)
  sketch-geometry (9):
    g0: LineSegment StartX=-7.00011 StartY=9.99951 StartZ=0 EndX=7.00011 EndY=9.99951 EndZ=0
    g1: LineSegment StartX=8.53192 StartY=8.5 StartZ=0 EndX=8.53192 EndY=4.50006 EndZ=0
    g2: LineSegment StartX=7.00011 StartY=3.00002 StartZ=0 EndX=-7.00011 EndY=3.00002 EndZ=0
    g3: LineSegment StartX=-8.53192 StartY=4.50006 StartZ=0 EndX=-8.53192 EndY=8.5 EndZ=0
    g4: ArcOfCircle CenterX=-7.03208 CenterY=8.50001 CenterZ=0 NormalX=0 NormalY=0 NormalZ=1 Radius=1.49984 StartAngle=1.54948 EndAngle=3.1416
    g5: ArcOfCircle CenterX=7.03208 CenterY=8.50001 CenterZ=0 NormalX=0 NormalY=0 NormalZ=1 Radius=1.49984 StartAngle=6.28318 EndAngle=7.8753
    g6: ArcOfCircle CenterX=7.00011 CenterY=4.53216 CenterZ=0 NormalX=0 NormalY=0 NormalZ=1 Radius=1.53215 StartAngle=4.71239 EndAngle=6.26223
    g7: ArcOfCircle CenterX=-7.00011 CenterY=4.53216 CenterZ=0 NormalX=0 NormalY=0 NormalZ=1 Radius=1.53215 StartAngle=3.16255 EndAngle=4.71239
    g8: LineSegment StartX=-8.53192 StartY=6.49976 StartZ=0 EndX=8.53192 EndY=6.49976 EndZ=0
  constraints (18):
    c: Coincident(g4,g3)
    c: Coincident(g7,g3)
    c: Coincident(g7,g2)
    c: Coincident(g6,g2)
    c: Coincident(g5,g1)
    c: Coincident(g1,g6)
    c: Coincident(g4,g0)
    c: Coincident(g0,g5)
    c: Parallel(g0,g2)
    c: Parallel(g3,g1)
    c: Symmetric(g3,g1,g-2)
    c: Symmetric(g3,g1,g-2)
    c: Symmetric(g0,g0,g-2)
    c: PointOnObject(g8,g3)
    c: PointOnObject(g8,g1)
    c: Horizontal(g8)
    c: Symmetric(g0,g2,g8)
    c: Symmetric(g0,g2,g8)
FEATURE [PartDesign::Pad] Pad020  label="back_hole"
  Length = 10
  Length2 = 100
  Placement = pos=(0,45,0) rot=(0,0.707107,0.707107;3.14159rad)
  Reversed = true
  Sketch = -> Sketch017
  Type = 0
FEATURE [Part::Cylinder] Cylinder  label="Cilindro015"
  Angle = 360
  Height = 30
  Placement = pos=(-26,39.75,-10) rot=(0,0,1;0rad)
  Radius = 1.75
FEATURE [Part::Box] Box011  label="Cubo011"
  Height = 10
  Length = 7
  Placement = pos=(-16,28.5,0) rot=(0,0,1;0rad)
  Width = 6
FEATURE [Part::Fillet] Fillet006  label="screw_tunnel"
  Base = -> Box011
  Edges = 1 edges r=1: [Edge5]
  Placement = pos=(-13,9,0) rot=(0,0,1;0rad)
FEATURE [Sketcher::SketchObject] Sketch018
  Placement = pos=(0,0,40) rot=(0,0,1;0rad)
  sketch-geometry (8):
    g0: LineSegment StartX=-7 StartY=7 StartZ=0 EndX=7 EndY=7 EndZ=0
    g1: LineSegment StartX=8.5 StartY=5.5 StartZ=0 EndX=8.5 EndY=-16.5 EndZ=0
    g2: LineSegment StartX=7 StartY=-18 StartZ=0 EndX=-7 EndY=-18 EndZ=0
    g3: LineSegment StartX=-8.5 StartY=-16.5 StartZ=0 EndX=-8.5 EndY=5.5 EndZ=0
    g4: ArcOfCircle CenterX=-7 CenterY=-16.5 CenterZ=0 NormalX=0 NormalY=0 NormalZ=1 Radius=1.5 StartAngle=3.14159 EndAngle=4.71239
    g5: ArcOfCircle CenterX=-7 CenterY=5.5 CenterZ=0 NormalX=0 NormalY=0 NormalZ=1 Radius=1.5 StartAngle=1.5708 EndAngle=3.14159
    g6: ArcOfCircle CenterX=7 CenterY=5.5 CenterZ=0 NormalX=0 NormalY=0 NormalZ=1 Radius=1.5 StartAngle=0 EndAngle=1.5708
    g7: ArcOfCircle CenterX=7 CenterY=-16.5 CenterZ=0 NormalX=0 NormalY=0 NormalZ=1 Radius=1.5 StartAngle=4.71239 EndAngle=6.28319
  constraints (19):
    c: Horizontal(g0)
    c: Horizontal(g2)
    c: Vertical(g1)
    c: Vertical(g3)
    c: Tangent(g3,g4) = 1.5708
    c: Tangent(g2,g4) = 1.5708
    c: Tangent(g3,g5) = 1.5708
    c: Tangent(g0,g5) = 1.5708
    c: Tangent(g0,g6) = 1.5708
    c: Tangent(g1,g6) = 1.5708
    c: Tangent(g2,g7) = 1.5708
    c: Tangent(g1,g7) = 1.5708
    c: DistanceY(g-1,g0) = 7
    c: DistanceY(g0,g2) = -25
    c: DistanceX(g3,g1) = 17
    c: Symmetric(g3,g1,g-2)
    c: Equal(g0,g2)
    c: Equal(g3,g1)
    c: Radius(g5) = 1.5
FEATURE [PartDesign::Pad] Pad021
  Length = 35
  Length2 = 100
  Placement = pos=(0,0,40) rot=(0,0,1;0rad)
  Reversed = true
  Sketch = -> Sketch018
  Type = 0
FEATURE [Part::Cut] Cut023
  Base = -> Cut006
  Tool = -> Pad021
FEATURE [Part::Cone] Cone  label="Cono"
  Angle = 360
  Height = 3
  Placement = pos=(-26,-38.75,-4) rot=(0,0,1;0rad)
  Radius1 = 3.8
  Radius2 = 1
FEATURE [Part::Cylinder] Cylinder018  label="cover_holes"
  Angle = 360
  Height = 108
  Placement = pos=(-54,0,18) rot=(0,1,0;1.5708rad)
  Radius = 1.75
FEATURE [Part::Box] Box012  label="Cubo012"
  Height = 10
  Length = 12
  Placement = pos=(-6,30,22) rot=(0,0,1;0rad)
  Width = 16
FEATURE [Part::Cut] Cut027
  Base = -> Cut023
  Tool = -> Box012
FEATURE [Part::Box] Box013  label="Cubo013"
  Height = 11
  Length = 6
  Placement = pos=(-28.75,-4.5,14) rot=(0,0,1;0rad)
  Width = 9
FEATURE [Part::Cylinder] Cylinder019  label="Cilindro016"
  Angle = 360
  Height = 68
  Placement = pos=(-34,0,18) rot=(0,1,0;1.5708rad)
  Radius = 1.75
FEATURE [Part::Cut] Cut028
  Base = -> Box013
  Tool = -> Cylinder019
FEATURE [Part::Chamfer] Chamfer008
  Base = -> Cut028
  Edges = 1 edges r=1.5: [Edge3]
FEATURE [Part::Fillet] Fillet009
  Base = -> Chamfer008
  Edges = 2 edges r=1.5: [Edge6,Edge14]
FEATURE [Part::Prism] Prism010  label="Prisma010"
  Circumradius = 3.25
  Height = 10
  Placement = pos=(-17.5,0,18) rot=(-0.250563,-0.935113,0.250563;1.63783rad)
  Polygon = 6
FEATURE [Part::Cut] Cut029
  Base = -> Fillet009
  Tool = -> Prism010
FEATURE [Part::Box] Box014  label="Cubo014"
  Height = 3
  Length = 4
  Placement = pos=(-29.75,-4.5,23) rot=(0,0,1;0rad)
  Width = 9
FEATURE [Part::MultiFuse] Fusion016
  Shapes = -> [Cut029,Box014]
FEATURE [Part::Mirroring] Part__Mirroring032  label="Fusion016 (Mirror #31)"
  Base = (0,0,0)
  Normal = (1,0,0)
  Source = -> Fusion016
FEATURE [Part::MultiFuse] Fusion017
  Shapes = -> [Fusion016,Part__Mirroring032]
FEATURE [Part::MultiFuse] Fusion018
  Shapes = -> [Cut027,Fusion017]
FEATURE [Part::Fillet] Fillet010  label="prebodyA"
  Base = -> Fusion018
  Edges = 9 edges r=0.5: [Edge41,Edge73,Edge125,Edge126,Edge127,Edge149,Edge151,Edge152,Edge153]
FEATURE [Part::FeaturePython] Clone015  label="Clone of bodyB"  # WARN: FeaturePython — macro-defined, semantics opaque (R4)
  Scale = (1,1,1)
FEATURE [App::DocumentObjectGroup] Grupo009  label="eyes"
  Group = -> [Pad016,Pad017,Fillet004,Pad018,Fillet005,Pad019]
FEATURE [Part::FeaturePython] Clone017  label="Clone of legB"  # WARN: FeaturePython — macro-defined, semantics opaque (R4)
  Scale = (1,1,1)
FEATURE [Part::Mirroring] Part__Mirroring033  label="Clone of legB (Mirror #29)"
  Base = (0,0,0)
  Normal = (1,0,0)
  Source = -> Clone017
FEATURE [Part::Mirroring] Part__Mirroring034  label="Clone of legB (Mirror #30)"
  Base = (0,0,0)
  Normal = (0,1,0)
  Source = -> Clone017
FEATURE [Part::Mirroring] Part__Mirroring035  label="Clone of legB (Mirror #31)"
  Base = (0,0,0)
  Normal = (0,1,0)
  Source = -> Part__Mirroring033
FEATURE [Part::Cylinder] Cylinder020
  Angle = 360
  Height = 10
  Placement = pos=(0,0,-4) rot=(0,0,1;0rad)
  Radius = 1.5
FEATURE [Part::MultiFuse] Fusion020
FEATURE [Part::Cut] Cut031  label="bearing"
  Base = -> Fusion020
  Tool = -> Cylinder020
FEATURE [Part::FeaturePython] Clone018  label="Clone of bearing"  # Draft clone (typed FeaturePython)
  Objects = -> [Cut031]
  Placement = pos=(23,23,33) rot=(1,0,0;3.14159rad)
  Scale = (1,1,1)
FEATURE [Part::FeaturePython] Clone019  label="Clone of bearing001"  # Draft clone (typed FeaturePython)
  Objects = -> [Cut031]
  Placement = pos=(47,-10,7) rot=(0,-0.707107,0.707107;3.14159rad)
  Scale = (1,1,1)
FEATURE [Part::Cylinder] Cylinder021  label="Cilindro017"
  Angle = 360
  Height = 15
  Placement = pos=(-7,26,17) rot=(0,0,1;0rad)
  Radius = 2
FEATURE [Part::Cut] Cut032  label="bodyA"
  Base = -> Fillet010
  Tool = -> Cylinder021
FEATURE [Part::FeaturePython] Clone020  label="Clone of bodyA"  # Draft clone (typed FeaturePython)
  Objects = -> [Cut032]
  Scale = (1,1,1)
FEATURE [App::DocumentObjectGroup] Grupo008  label="chassis"
  Group = -> [Clone015,Clone020]
FEATURE [Sketcher::SketchObject] Sketch021
  Placement = pos=(0,0,29) rot=(0,0,1;0rad)
  sketch-geometry (2):
    g0: Circle CenterX=-23 CenterY=23 CenterZ=0 NormalX=0 NormalY=0 NormalZ=1 Radius=4.5
    g1: Circle CenterX=-23 CenterY=23 CenterZ=0 NormalX=0 NormalY=0 NormalZ=1 Radius=8.5
  constraints (5):
    c: Radius(g0) = 4.5
    c: Coincident(g1,g0)
    c: Radius(g1) = 8.5
    c: DistanceY(g-1,g0) = 23
    c: DistanceX(g-1,g0) = -23
FEATURE [PartDesign::Pad] Pad023  label="spacer"
  Length = 1
  Length2 = 100
  Placement = pos=(0,0,29) rot=(0,0,1;0rad)
  Sketch = -> Sketch021
  Type = 0
FEATURE [Part::FeaturePython] Clone021  label="Clone of spacer"  # Draft clone (typed FeaturePython)
  Objects = -> [Pad023]
  Placement = pos=(0,0,29) rot=(0,0,1;0rad)
  Scale = (1,1,1)
FEATURE [Part::Mirroring] Part__Mirroring042  label="Clone of spacer (Mirror #38)"
  Base = (0,0,0)
  Normal = (0,1,0)
  Source = -> Clone021
FEATURE [Part::Mirroring] Part__Mirroring043  label="Clone of spacer (Mirror #39)"
  Base = (0,0,0)
  Normal = (1,0,0)
  Source = -> Clone021
FEATURE [Part::Mirroring] Part__Mirroring044  label="Clone of spacer (Mirror #40)"
  Base = (0,0,0)
  Normal = (1,0,0)
  Source = -> Part__Mirroring042
FEATURE [App::DocumentObjectGroup] Grupo007  label="legs"
  Group = -> [Part__Mirroring018,Part__Mirroring019,Part__Mirroring021,Part__Mirroring022,Part__Mirroring023,Part__Mirroring025,Part__Mirroring034,Part__Mirroring035,Part__Mirroring043,Part__Mirroring044]
FEATURE [Part::Feature] Part__Feature001  label="Nyloc-nut-M3"
  shape: bbox 6.35 x 6.35 x 3.86 mm, 32 faces (baked)
FEATURE [Part::Feature] Part__Feature002  label="Nyloc-nut-M004"
  shape: bbox 3.5 x 3.5 x 0.95 mm, 4 faces (baked)
FEATURE [Part::MultiFuse] Fusion  label="m3-nyloc-nut"
  Shapes = -> [Part__Feature001,Part__Feature002]
FEATURE [Part::Feature] Part__Feature003  label="m3-nut"
  Placement = pos=(0,0,0) rot=(0,0,1;0.523599rad)
  shape: bbox 6.35 x 6.35 x 2.4 mm, 29 faces (baked)
FEATURE [Part::Feature] Part__Feature004  label="hex-bolt"
  shape: bbox 5.5 x 5.5 x 13 mm, 16 faces (baked)
FEATURE [Part::Feature] Fusion022  label="hex-m3-30mm"
  shape: bbox 5.5 x 5.5 x 33 mm, 16 faces (baked)
FEATURE [Part::Feature] Chamfer010  label="hex-m3-8mm"
  Placement = pos=(160,0,0) rot=(0,0,1;0rad)
  shape: bbox 5.5 x 5.5 x 11 mm, 16 faces (baked)
FEATURE [Part::Feature] Chamfer013  label="hex-m2-4mm"
  shape: bbox 5.445 x 6.287 x 6.3 mm, 16 faces (baked)
FEATURE [Part::FeaturePython] Clone022  label="Clone of hex-m3-8mm"  # Draft clone (typed FeaturePython)
  Objects = -> [Chamfer010]
  Placement = pos=(23,-23,32.9) rot=(0,0,1;0rad)
  Scale = (1,1,1)
FEATURE [Part::FeaturePython] Clone023  label="Clone of hex-m3-8mm001"  # Draft clone (typed FeaturePython)
  Objects = -> [Chamfer010]
  Placement = pos=(-47,-10,6.9) rot=(-1,0,0;1.5708rad)
  Scale = (1,1,1)
FEATURE [Part::FeaturePython] Clone024  label="Clone of hex-m3-8mm002"  # Draft clone (typed FeaturePython)
  Objects = -> [Chamfer010]
  Placement = pos=(-23,23,32.9) rot=(0,0,1;0rad)
  Scale = (1,1,1)
FEATURE [Part::FeaturePython] Clone025  label="Clone of hex-m3-8mm003"  # Draft clone (typed FeaturePython)
  Objects = -> [Chamfer010]
  Placement = pos=(-31,0,17.9) rot=(0,-1,0;1.5708rad)
  Scale = (1,1,1)
FEATURE [Part::FeaturePython] Clone026  label="Clone of hex-m3-8mm004"  # Draft clone (typed FeaturePython)
  Objects = -> [Chamfer010]
  Placement = pos=(31,0,17.9) rot=(0,1,0;1.5708rad)
  Scale = (1,1,1)
FEATURE [Part::FeaturePython] Clone027  label="Clone of hex-m3-8mm005"  # Draft clone (typed FeaturePython)
  Objects = -> [Chamfer010]
  Placement = pos=(47,10,6.9) rot=(1,0,0;1.5708rad)
  Scale = (1,1,1)
FEATURE [Part::FeaturePython] Clone028  label="Clone of hex-m3-8mm006"  # Draft clone (typed FeaturePython)
  Objects = -> [Chamfer010]
  Placement = pos=(-47,10,6.9) rot=(1,0,0;1.5708rad)
  Scale = (1,1,1)
FEATURE [Part::FeaturePython] Clone029  label="Clone of hex-m3-8mm007"  # Draft clone (typed FeaturePython)
  Objects = -> [Chamfer010]
  Placement = pos=(23,23,32.9) rot=(0,0,1;0rad)
  Scale = (1,1,1)
FEATURE [Part::FeaturePython] Clone030  label="Clone of hex-m3-8mm008"  # Draft clone (typed FeaturePython)
  Objects = -> [Chamfer010]
  Placement = pos=(47,-10,6.9) rot=(-1,0,0;1.5708rad)
  Scale = (1,1,1)
FEATURE [Part::FeaturePython] Clone031  label="Clone of hex-m3-8mm009"  # Draft clone (typed FeaturePython)
  Objects = -> [Chamfer010]
  Placement = pos=(-23,-23,32.9) rot=(0,0,1;0rad)
  Scale = (1,1,1)
FEATURE [Part::FeaturePython] Clone032  label="Clone of hex-m3-30mm"  # Draft clone (typed FeaturePython)
  Objects = -> [Fusion022]
  Placement = pos=(-89,-37.9,-3) rot=(1,0,0;1.5708rad)
  Scale = (1,1,1)
FEATURE [Part::FeaturePython] Clone033  label="Clone of hex-m3-30mm001"  # Draft clone (typed FeaturePython)
  Objects = -> [Fusion022]
  Placement = pos=(101,37.9,19) rot=(-1,0,0;1.5708rad)
  Scale = (1,1,1)
FEATURE [Part::FeaturePython] Clone034  label="Clone of hex-m3-30mm002"  # Draft clone (typed FeaturePython)
  Objects = -> [Fusion022]
  Placement = pos=(-101,-37.9,19) rot=(1,0,0;1.5708rad)
  Scale = (1,1,1)
FEATURE [Part::FeaturePython] Clone035  label="Clone of hex-m3-30mm003"  # Draft clone (typed FeaturePython)
  Objects = -> [Fusion022]
  Placement = pos=(-89,37.9,-3) rot=(-1,0,0;1.5708rad)
  Scale = (1,1,1)
FEATURE [Part::FeaturePython] Clone036  label="Clone of hex-m3-30mm004"  # Draft clone (typed FeaturePython)
  Objects = -> [Fusion022]
  Placement = pos=(-59,-37.9,29) rot=(1,0,0;1.5708rad)
  Scale = (1,1,1)
FEATURE [Part::FeaturePython] Clone037  label="Clone of hex-m3-30mm005"  # Draft clone (typed FeaturePython)
  Objects = -> [Fusion022]
  Placement = pos=(-59,37.9,29) rot=(-1,0,0;1.5708rad)
  Scale = (1,1,1)
FEATURE [Part::FeaturePython] Clone038  label="Clone of hex-m3-30mm006"  # Draft clone (typed FeaturePython)
  Objects = -> [Fusion022]
  Placement = pos=(59,37.9,29) rot=(-1,0,0;1.5708rad)
  Scale = (1,1,1)
FEATURE [Part::FeaturePython] Clone039  label="Clone of hex-m3-30mm007"  # Draft clone (typed FeaturePython)
  Objects = -> [Fusion022]
  Placement = pos=(89,-37.9,-3) rot=(1,0,0;1.5708rad)
  Scale = (1,1,1)
FEATURE [Part::FeaturePython] Clone040  label="Clone of hex-m3-30mm008"  # Draft clone (typed FeaturePython)
  Objects = -> [Fusion022]
  Placement = pos=(89,37.9,-3) rot=(-1,0,0;1.5708rad)
  Scale = (1,1,1)
FEATURE [Part::FeaturePython] Clone041  label="Clone of hex-m3-30mm009"  # Draft clone (typed FeaturePython)
  Objects = -> [Fusion022]
  Placement = pos=(101,-37.9,19) rot=(1,0,0;1.5708rad)
  Scale = (1,1,1)
FEATURE [Part::FeaturePython] Clone042  label="Clone of hex-m3-30mm010"  # Draft clone (typed FeaturePython)
  Objects = -> [Fusion022]
  Placement = pos=(59,-37.9,29) rot=(1,0,0;1.5708rad)
  Scale = (1,1,1)
FEATURE [Part::FeaturePython] Clone043  label="Clone of hex-m3-30mm011"  # Draft clone (typed FeaturePython)
  Objects = -> [Fusion022]
  Placement = pos=(-101,37.9,19) rot=(-1,0,0;1.5708rad)
  Scale = (1,1,1)
FEATURE [Part::FeaturePython] Clone044  label="Clone of hex-m2-4mm"  # Draft clone (typed FeaturePython)
  Objects = -> [Chamfer013]
  Placement = pos=(47.0481,-51.1815,7.03289) rot=(1,0,0;1.5708rad)
  Scale = (1,1,1)
FEATURE [Part::FeaturePython] Clone045  label="Clone of hex-m2-4mm001"  # Draft clone (typed FeaturePython)
  Objects = -> [Chamfer013]
  Placement = pos=(-47.1019,51.0089,7.03289) rot=(-1,0,0;1.5708rad)
  Scale = (1,1,1)
FEATURE [Part::FeaturePython] Clone046  label="Clone of hex-m2-4mm002"  # Draft clone (typed FeaturePython)
  Objects = -> [Chamfer013]
  Placement = pos=(47.006,51.0807,7.03289) rot=(-1,0,0;1.5708rad)
  Scale = (1,1,1)
FEATURE [Part::FeaturePython] Clone047  label="Clone of hex-m2-4mm003"  # Draft clone (typed FeaturePython)
  Objects = -> [Chamfer013]
  Placement = pos=(-47.0425,-51.021,7.03289) rot=(1,0,0;1.5708rad)
  Scale = (1,1,1)
FEATURE [Part::Feature] Chamfer018  label="hex-m2-6mm"
  shape: bbox 5.445 x 6.287 x 7.5 mm, 16 faces (baked)
FEATURE [App::DocumentObjectGroup] Grupo011  label="bolts and nuts"
  Group = -> [Chamfer010,Fusion,Part__Feature003,Part__Feature004,Fusion022,Chamfer013,Chamfer018]
FEATURE [Part::FeaturePython] Clone063  label="Clone of hex-m2-6mm015"  # Draft clone (typed FeaturePython)
  Objects = -> [Chamfer018]
  Placement = pos=(-26.75,-31.3,3.25) rot=(0,0,1;0rad)
  Scale = (1,1,1)
FEATURE [Part::FeaturePython] Clone064  label="Clone of hex-m2-6mm014"  # Draft clone (typed FeaturePython)
  Objects = -> [Chamfer018]
  Placement = pos=(-19.25,-31.3,3.25) rot=(0,0,1;0rad)
  Scale = (1,1,1)
FEATURE [Part::FeaturePython] Clone065  label="Clone of hex-m2-6mm013"  # Draft clone (typed FeaturePython)
  Objects = -> [Chamfer018]
  Placement = pos=(19.25,-31.3,3.25) rot=(0,0,1;0rad)
  Scale = (1,1,1)
FEATURE [Part::FeaturePython] Clone066  label="Clone of hex-m2-6mm012"  # Draft clone (typed FeaturePython)
  Objects = -> [Chamfer018]
  Placement = pos=(26.75,-31.3,3.25) rot=(0,0,1;0rad)
  Scale = (1,1,1)
FEATURE [Part::FeaturePython] Clone067  label="Clone of hex-m2-6mm011"  # Draft clone (typed FeaturePython)
  Objects = -> [Chamfer018]
  Placement = pos=(-26.75,31.3,3.25) rot=(0,0,1;0rad)
  Scale = (1,1,1)
FEATURE [Part::FeaturePython] Clone068  label="Clone of hex-m2-6mm010"  # Draft clone (typed FeaturePython)
  Objects = -> [Chamfer018]
  Placement = pos=(-19.25,31.3,3.25) rot=(0,0,1;0rad)
  Scale = (1,1,1)
FEATURE [Part::FeaturePython] Clone069  label="Clone of hex-m2-6mm009"  # Draft clone (typed FeaturePython)
  Objects = -> [Chamfer018]
  Placement = pos=(19.25,31.3,3.25) rot=(0,0,1;0rad)
  Scale = (1,1,1)
FEATURE [Part::FeaturePython] Clone070  label="Clone of hex-m2-6mm008"  # Draft clone (typed FeaturePython)
  Objects = -> [Chamfer018]
  Placement = pos=(26.75,31.3,3.25) rot=(0,0,1;0rad)
  Scale = (1,1,1)
FEATURE [Part::FeaturePython] Clone071  label="Clone of hex-m2-6mm007"  # Draft clone (typed FeaturePython)
  Objects = -> [Chamfer018]
  Placement = pos=(-26.75,-3.3,3.25) rot=(0,0,1;0rad)
  Scale = (1,1,1)
FEATURE [Part::FeaturePython] Clone072  label="Clone of hex-m2-6mm006"  # Draft clone (typed FeaturePython)
  Objects = -> [Chamfer018]
  Placement = pos=(-19.25,-3.3,3.25) rot=(0,0,1;0rad)
  Scale = (1,1,1)
FEATURE [Part::FeaturePython] Clone073  label="Clone of hex-m2-6mm005"  # Draft clone (typed FeaturePython)
  Objects = -> [Chamfer018]
  Placement = pos=(19.25,-3.3,3.25) rot=(0,0,1;0rad)
  Scale = (1,1,1)
FEATURE [Part::FeaturePython] Clone074  label="Clone of hex-m2-6mm004"  # Draft clone (typed FeaturePython)
  Objects = -> [Chamfer018]
  Placement = pos=(26.75,-3.3,3.25) rot=(0,0,1;0rad)
  Scale = (1,1,1)
FEATURE [Part::FeaturePython] Clone075  label="Clone of hex-m2-6mm003"  # Draft clone (typed FeaturePython)
  Objects = -> [Chamfer018]
  Placement = pos=(-26.75,3.3,3.25) rot=(0,0,1;0rad)
  Scale = (1,1,1)
FEATURE [Part::FeaturePython] Clone076  label="Clone of hex-m2-6mm002"  # Draft clone (typed FeaturePython)
  Objects = -> [Chamfer018]
  Placement = pos=(-19.25,3.3,3.25) rot=(0,0,1;0rad)
  Scale = (1,1,1)
FEATURE [Part::FeaturePython] Clone077  label="Clone of hex-m2-6mm001"  # Draft clone (typed FeaturePython)
  Objects = -> [Chamfer018]
  Placement = pos=(19.25,3.3,3.25) rot=(0,0,1;0rad)
  Scale = (1,1,1)
FEATURE [Part::FeaturePython] Clone078  label="Clone of hex-m2-6mm"  # Draft clone (typed FeaturePython)
  Objects = -> [Chamfer018]
  Placement = pos=(26.75,3.3,3.25) rot=(0,0,1;0rad)
  Scale = (1,1,1)
FEATURE [Part::FeaturePython] Clone079  label="Clone of hex-m2-6mm016"  # Draft clone (typed FeaturePython)
  Objects = -> [Chamfer018]
  Placement = pos=(-43.25,-39.3,26.7) rot=(1,0,0;1.5708rad)
  Scale = (1,1,1)
FEATURE [Part::FeaturePython] Clone080  label="Clone of hex-m2-6mm017"  # Draft clone (typed FeaturePython)
  Objects = -> [Chamfer018]
  Placement = pos=(50.75,-39.3,26.7) rot=(1,0,0;1.5708rad)
  Scale = (1,1,1)
FEATURE [Part::FeaturePython] Clone081  label="Clone of hex-m2-6mm018"  # Draft clone (typed FeaturePython)
  Objects = -> [Chamfer018]
  Placement = pos=(43.25,-39.3,26.7) rot=(1,0,0;1.5708rad)
  Scale = (1,1,1)
FEATURE [Part::FeaturePython] Clone082  label="Clone of hex-m2-6mm019"  # Draft clone (typed FeaturePython)
  Objects = -> [Chamfer018]
  Placement = pos=(-50.75,-39.3,26.7) rot=(1,0,0;1.5708rad)
  Scale = (1,1,1)
FEATURE [Part::FeaturePython] Clone083  label="Clone of hex-m2-6mm020"  # Draft clone (typed FeaturePython)
  Objects = -> [Chamfer018]
  Placement = pos=(-43.25,-39.3,-1.3) rot=(1,0,0;1.5708rad)
  Scale = (1,1,1)
FEATURE [Part::FeaturePython] Clone084  label="Clone of hex-m2-6mm021"  # Draft clone (typed FeaturePython)
  Objects = -> [Chamfer018]
  Placement = pos=(50.75,-39.3,-1.3) rot=(1,0,0;1.5708rad)
  Scale = (1,1,1)
FEATURE [Part::FeaturePython] Clone085  label="Clone of hex-m2-6mm022"  # Draft clone (typed FeaturePython)
  Objects = -> [Chamfer018]
  Placement = pos=(43.25,-39.3,-1.3) rot=(1,0,0;1.5708rad)
  Scale = (1,1,1)
FEATURE [Part::FeaturePython] Clone086  label="Clone of hex-m2-6mm023"  # Draft clone (typed FeaturePython)
  Objects = -> [Chamfer018]
  Placement = pos=(-50.75,-39.3,-1.3) rot=(1,0,0;1.5708rad)
  Scale = (1,1,1)
FEATURE [Part::FeaturePython] Clone087  label="Clone of hex-m2-6mm024"  # Draft clone (typed FeaturePython)
  Objects = -> [Chamfer018]
  Placement = pos=(43.25,39.3,26.7) rot=(0,0.707107,0.707107;3.14159rad)
  Scale = (1,1,1)
FEATURE [Part::FeaturePython] Clone088  label="Clone of hex-m2-6mm025"  # Draft clone (typed FeaturePython)
  Objects = -> [Chamfer018]
  Placement = pos=(-50.75,39.3,26.7) rot=(0,0.707107,0.707107;3.14159rad)
  Scale = (1,1,1)
FEATURE [Part::FeaturePython] Clone089  label="Clone of hex-m2-6mm026"  # Draft clone (typed FeaturePython)
  Objects = -> [Chamfer018]
  Placement = pos=(-43.25,39.3,26.7) rot=(0,0.707107,0.707107;3.14159rad)
  Scale = (1,1,1)
FEATURE [Part::FeaturePython] Clone090  label="Clone of hex-m2-6mm027"  # Draft clone (typed FeaturePython)
  Objects = -> [Chamfer018]
  Placement = pos=(50.75,39.3,26.7) rot=(0,0.707107,0.707107;3.14159rad)
  Scale = (1,1,1)
FEATURE [Part::FeaturePython] Clone091  label="Clone of hex-m2-6mm028"  # Draft clone (typed FeaturePython)
  Objects = -> [Chamfer018]
  Placement = pos=(43.25,39.3,-1.3) rot=(0,0.707107,0.707107;3.14159rad)
  Scale = (1,1,1)
FEATURE [Part::FeaturePython] Clone092  label="Clone of hex-m2-6mm029"  # Draft clone (typed FeaturePython)
  Objects = -> [Chamfer018]
  Placement = pos=(-50.75,39.3,-1.3) rot=(0,0.707107,0.707107;3.14159rad)
  Scale = (1,1,1)
FEATURE [Part::FeaturePython] Clone093  label="Clone of hex-m2-6mm030"  # Draft clone (typed FeaturePython)
  Objects = -> [Chamfer018]
  Placement = pos=(-43.25,39.3,-1.3) rot=(0,0.707107,0.707107;3.14159rad)
  Scale = (1,1,1)
FEATURE [Part::FeaturePython] Clone094  label="Clone of hex-m2-6mm031"  # Draft clone (typed FeaturePython)
  Objects = -> [Chamfer018]
  Placement = pos=(50.75,39.3,-1.3) rot=(0,0.707107,0.707107;3.14159rad)
  Scale = (1,1,1)
FEATURE [Part::FeaturePython] Clone095  label="Clone of m3-nut"  # Draft clone (typed FeaturePython)
  Objects = -> [Part__Feature003]
  Placement = pos=(47,-15.5,7) rot=(0.935113,-0.250563,0.250563;1.63783rad)
  Scale = (1,1,1)
FEATURE [Part::FeaturePython] Clone096  label="Clone of m3-nut001"  # Draft clone (typed FeaturePython)
  Objects = -> [Part__Feature003]
  Placement = pos=(-47,-15.5,7) rot=(0.935113,-0.250563,0.250563;1.63783rad)
  Scale = (1,1,1)
FEATURE [Part::FeaturePython] Clone097  label="Clone of m3-nut002"  # Draft clone (typed FeaturePython)
  Objects = -> [Part__Feature003]
  Placement = pos=(47,17.9,7) rot=(0.935113,-0.250563,0.250563;1.63783rad)
  Scale = (1,1,1)
FEATURE [Part::FeaturePython] Clone098  label="Clone of m3-nut003"  # Draft clone (typed FeaturePython)
  Objects = -> [Part__Feature003]
  Placement = pos=(-47,17.9,7) rot=(0.935113,-0.250563,0.250563;1.63783rad)
  Scale = (1,1,1)
FEATURE [Part::FeaturePython] Clone099  label="Clone of m3-nyloc-nut"  # Draft clone (typed FeaturePython)
  Objects = -> [Fusion]
  Placement = pos=(-101,14,19) rot=(0,-0.707107,0.707107;3.14159rad)
  Scale = (1,1,1)
FEATURE [Part::FeaturePython] Clone100  label="Clone of m3-nyloc-nut001"  # Draft clone (typed FeaturePython)
  Objects = -> [Fusion]
  Placement = pos=(-89,14,-3) rot=(0,-0.707107,0.707107;3.14159rad)
  Scale = (1,1,1)
FEATURE [Part::FeaturePython] Clone101  label="Clone of m3-nyloc-nut002"  # Draft clone (typed FeaturePython)
  Objects = -> [Fusion]
  Placement = pos=(-59,14,29) rot=(0,-0.707107,0.707107;3.14159rad)
  Scale = (1,1,1)
FEATURE [Part::FeaturePython] Clone102  label="Clone of m3-nyloc-nut003"  # Draft clone (typed FeaturePython)
  Objects = -> [Fusion]
  Placement = pos=(101,-14,19) rot=(-1,0,0;1.5708rad)
  Scale = (1,1,1)
FEATURE [Part::FeaturePython] Clone103  label="Clone of m3-nyloc-nut004"  # Draft clone (typed FeaturePython)
  Objects = -> [Fusion]
  Placement = pos=(59,-14,29) rot=(-1,0,0;1.5708rad)
  Scale = (1,1,1)
FEATURE [Part::FeaturePython] Clone104  label="Clone of m3-nyloc-nut005"  # Draft clone (typed FeaturePython)
  Objects = -> [Fusion]
  Placement = pos=(89,14,-3) rot=(0,-0.707107,0.707107;3.14159rad)
  Scale = (1,1,1)
FEATURE [Part::FeaturePython] Clone105  label="Clone of m3-nyloc-nut006"  # Draft clone (typed FeaturePython)
  Objects = -> [Fusion]
  Placement = pos=(59,14,29) rot=(0,-0.707107,0.707107;3.14159rad)
  Scale = (1,1,1)
FEATURE [Part::FeaturePython] Clone106  label="Clone of m3-nyloc-nut007"  # Draft clone (typed FeaturePython)
  Objects = -> [Fusion]
  Placement = pos=(101,14,19) rot=(0,-0.707107,0.707107;3.14159rad)
  Scale = (1,1,1)
FEATURE [Part::FeaturePython] Clone107  label="Clone of m3-nyloc-nut008"  # Draft clone (typed FeaturePython)
  Objects = -> [Fusion]
  Placement = pos=(89,-14,-3) rot=(-1,0,0;1.5708rad)
  Scale = (1,1,1)
FEATURE [Part::FeaturePython] Clone108  label="Clone of m3-nyloc-nut009"  # Draft clone (typed FeaturePython)
  Objects = -> [Fusion]
  Placement = pos=(-59,-14,29) rot=(-1,0,0;1.5708rad)
  Scale = (1,1,1)
FEATURE [Part::FeaturePython] Clone109  label="Clone of m3-nyloc-nut010"  # Draft clone (typed FeaturePython)
  Objects = -> [Fusion]
  Placement = pos=(-89,-14,-3) rot=(-1,0,0;1.5708rad)
  Scale = (1,1,1)
FEATURE [Part::FeaturePython] Clone110  label="Clone of m3-nyloc-nut011"  # Draft clone (typed FeaturePython)
  Objects = -> [Fusion]
  Placement = pos=(-101,-14,19) rot=(-1,0,0;1.5708rad)
  Scale = (1,1,1)
FEATURE [Part::FeaturePython] Clone111  label="Clone of m3-nyloc-nut012"  # Draft clone (typed FeaturePython)
  Objects = -> [Fusion]
  Placement = pos=(27.5,0,18) rot=(0,-1,0;1.5708rad)
  Scale = (1,1,1)
FEATURE [Part::FeaturePython] Clone112  label="Clone of m3-nyloc-nut013"  # Draft clone (typed FeaturePython)
  Objects = -> [Fusion]
  Placement = pos=(-27.5,0,18) rot=(0.707107,0,0.707107;3.14159rad)
  Scale = (1,1,1)
FEATURE [Part::FeaturePython] Clone113  label="Clone of m3-nyloc-nut014"  # Draft clone (typed FeaturePython)
  Objects = -> [Fusion]
  Placement = pos=(23,-23,27) rot=(0.965926,0.258819,0;3.14159rad)
  Scale = (1,1,1)
FEATURE [Part::FeaturePython] Clone114  label="Clone of m3-nyloc-nut015"  # Draft clone (typed FeaturePython)
  Objects = -> [Fusion]
  Placement = pos=(23,23,27) rot=(0.965926,0.258819,0;3.14159rad)
  Scale = (1,1,1)
FEATURE [Part::FeaturePython] Clone115  label="Clone of m3-nyloc-nut016"  # Draft clone (typed FeaturePython)
  Objects = -> [Fusion]
  Placement = pos=(-23,23,27) rot=(0.965926,0.258819,0;3.14159rad)
  Scale = (1,1,1)
FEATURE [Part::FeaturePython] Clone116  label="Clone of m3-nyloc-nut017"  # Draft clone (typed FeaturePython)
  Objects = -> [Fusion]
  Placement = pos=(-23,-23,27) rot=(0.965926,0.258819,0;3.14159rad)
  Scale = (1,1,1)
FEATURE [App::DocumentObjectGroup] Grupo013  label="nuts"
  Group = -> [Clone095,Clone096,Clone097,Clone098,Clone099,Clone100,Clone101,Clone102,Clone103,Clone104,Clone106,Clone105,Clone107,Clone108,Clone109,Clone110,Clone111,Clone112,Clone113,Clone114,Clone115,Clone116]
FEATURE [Part::FeaturePython] Clone117  label="Clone of bearing002"  # Draft clone (typed FeaturePython)
  Objects = -> [Cut031]
  Placement = pos=(-23,23,33) rot=(1,0,0;3.14159rad)
  Scale = (1,1,1)
FEATURE [Part::FeaturePython] Clone118  label="Clone of bearing003"  # Draft clone (typed FeaturePython)
  Objects = -> [Cut031]
  Placement = pos=(23,-23,33) rot=(1,0,0;3.14159rad)
  Scale = (1,1,1)
FEATURE [Part::FeaturePython] Clone119  label="Clone of bearing004"  # Draft clone (typed FeaturePython)
  Objects = -> [Cut031]
  Placement = pos=(-23,-23,33) rot=(1,0,0;3.14159rad)
  Scale = (1,1,1)
FEATURE [Part::FeaturePython] Clone120  label="Clone of bearing005"  # Draft clone (typed FeaturePython)
  Objects = -> [Cut031]
  Placement = pos=(-47,-10,7) rot=(0,-0.707107,0.707107;3.14159rad)
  Scale = (1,1,1)
FEATURE [Part::FeaturePython] Clone121  label="Clone of bearing006"  # Draft clone (typed FeaturePython)
  Objects = -> [Cut031]
  Placement = pos=(-47,10,7) rot=(-1,0,0;1.5708rad)
  Scale = (1,1,1)
FEATURE [Part::FeaturePython] Clone122  label="Clone of bearing007"  # Draft clone (typed FeaturePython)
  Objects = -> [Cut031]
  Placement = pos=(47,10,7) rot=(-1,0,0;1.5708rad)
  Scale = (1,1,1)
FEATURE [App::DocumentObjectGroup] Grupo010  label="bearings"
  Group = -> [Clone018,Clone117,Clone118,Clone119,Clone019,Clone120,Clone121,Clone122]
FEATURE [Part::FeaturePython] Clone123  label="Clone of TGY-306G004"  # Draft clone (typed FeaturePython)
  Objects = -> [Solid001]
  Placement = pos=(-23,-23,23.3) rot=(1,0,0;3.14159rad)
  Scale = (1,1,1)
FEATURE [Part::FeaturePython] Clone124  label="Clone of TGY-306G005"  # Draft clone (typed FeaturePython)
  Objects = -> [Solid001]
  Placement = pos=(23,23,23.3) rot=(0,1,0;3.14159rad)
  Scale = (1,1,1)
FEATURE [Part::FeaturePython] Clone125  label="Clone of TGY-306G006"  # Draft clone (typed FeaturePython)
  Objects = -> [Solid001]
  Placement = pos=(23,-23,23.3) rot=(1,0,0;3.14159rad)
  Scale = (1,1,1)
FEATURE [Part::FeaturePython] Clone126  label="Clone of TGY-306G007"  # Draft clone (typed FeaturePython)
  Objects = -> [Solid001]
  Placement = pos=(-47,-18,7) rot=(0,-0.707107,0.707107;3.14159rad)
  Scale = (1,1,1)
FEATURE [Part::FeaturePython] Clone127  label="Clone of TGY-306G008"  # Draft clone (typed FeaturePython)
  Objects = -> [Solid001]
  Placement = pos=(-47,18,7) rot=(-1,0,0;1.5708rad)
  Scale = (1,1,1)
FEATURE [Part::FeaturePython] Clone128  label="Clone of TGY-306G009"  # Draft clone (typed FeaturePython)
  Objects = -> [Solid001]
  Placement = pos=(47,18,7) rot=(-1,0,0;1.5708rad)
  Scale = (1,1,1)
FEATURE [App::DocumentObjectGroup] Grupo004  label="servos"
  Group = -> [Clone005,Clone,Clone123,Clone124,Clone125,Clone126,Clone127,Clone128]
FEATURE [App::DocumentObjectGroup] Grupo014  label="electronic"
  Group = -> [Clone002]
FEATURE [Part::FeaturePython] Clone129  label="Clone of hex-m2-4mm004"  # Draft clone (typed FeaturePython)
  Objects = -> [Chamfer013]
  Placement = pos=(22.9737,-23.0298,-9) rot=(1,0,0;3.14159rad)
  Scale = (1,1,1)
FEATURE [Part::FeaturePython] Clone130  label="Clone of hex-m2-4mm005"  # Draft clone (typed FeaturePython)
  Objects = -> [Chamfer013]
  Placement = pos=(-22.9909,-23.0768,-9) rot=(1,0,0;3.14159rad)
  Scale = (1,1,1)
FEATURE [Part::FeaturePython] Clone131  label="Clone of hex-m2-4mm006"  # Draft clone (typed FeaturePython)
  Objects = -> [Chamfer013]
  Placement = pos=(-22.9747,22.9186,-9) rot=(1,0,0;3.14159rad)
  Scale = (1,1,1)
FEATURE [Part::FeaturePython] Clone132  label="Clone of hex-m2-4mm007"  # Draft clone (typed FeaturePython)
  Objects = -> [Chamfer013]
  Placement = pos=(22.9617,22.9712,-9) rot=(1,0,0;3.14159rad)
  Scale = (1,1,1)
FEATURE [App::DocumentObjectGroup] Grupo012  label="bolts"
  Group = -> [Clone022,Clone023,Clone024,Clone025,Clone026,Clone027,Clone028,Clone029,Clone030,Clone031,Clone032,Clone033,Clone034,Clone035,Clone036,Clone037,Clone038,Clone039,Clone040,Clone041,Clone042,Clone043,Clone044,Clone045,Clone046,Clone047,Clone063,Clone064,Clone065,Clone066,Clone067,Clone068,Clone069,Clone070,Clone071,Clone072,Clone073,Clone074,Clone075,Clone076,Clone077,Clone078,Clone079,Clone080,+18 more]
FEATURE [Part::Sphere] Sphere  label="Esfera"
  Angle1 = -90
  Angle2 = 90
  Angle3 = 360
  Radius = 85
FEATURE [Part::Box] Box015  label="Cubo015"
  Height = 185
  Length = 400
  Placement = pos=(-200,-200,-150) rot=(0,0,1;0rad)
  Width = 400
FEATURE [Part::Cut] Cut033
  Base = -> Sphere
  Tool = -> Box015
FEATURE [Part::Sphere] Sphere001  label="Esfera001"
  Angle1 = -90
  Angle2 = 90
  Angle3 = 360
  Radius = 82
FEATURE [Part::Cut] Cut034
  Base = -> Cut033
  Tool = -> Sphere001
FEATURE [Sketcher::SketchObject] Sketch022
  Placement = pos=(0,-40,0) rot=(1,0,0;1.5708rad)
  sketch-geometry (8):
    g0: LineSegment StartX=-31.5 StartY=12 StartZ=0 EndX=-35 EndY=12 EndZ=0
    g1: LineSegment StartX=-35 StartY=12 StartZ=0 EndX=-35 EndY=53.5 EndZ=0
    g2: LineSegment StartX=-35 StartY=53.5 StartZ=0 EndX=-31.5 EndY=53.5 EndZ=0
    g3: LineSegment StartX=-31.5 StartY=53.5 StartZ=0 EndX=-31.5 EndY=33.5 EndZ=0
    g4: LineSegment StartX=-31.5 StartY=33.5 StartZ=0 EndX=-20 EndY=33.5 EndZ=0
    g5: LineSegment StartX=-20 StartY=33.5 StartZ=0 EndX=-20 EndY=29 EndZ=0
    g6: LineSegment StartX=-20 StartY=29 StartZ=0 EndX=-31.5 EndY=29 EndZ=0
    g7: LineSegment StartX=-31.5 StartY=29 StartZ=0 EndX=-31.5 EndY=12 EndZ=0
  constraints (24):
    c: Horizontal(g0)
    c: Coincident(g0,g1)
    c: Vertical(g1)
    c: Coincident(g1,g2)
    c: Horizontal(g2)
    c: Coincident(g2,g3)
    c: Vertical(g3)
    c: Coincident(g3,g4)
    c: Horizontal(g4)
    c: Coincident(g4,g5)
    c: Vertical(g5)
    c: Coincident(g5,g6)
    c: Horizontal(g6)
    c: Coincident(g6,g7)
    c: Coincident(g7,g0)
    c: Vertical(g7)
    c: Distance(g0) = 3.5
    c: DistanceX(g-1,g0) = -35
    c: DistanceY(g7) = -17
    c: Distance(g4) = 11.5
    c: Distance(g3) = 20
    c: DistanceY(g-1,g0) = 12
    c: Equal(g2,g0)
    c: Distance(g5) = 4.5
FEATURE [Sketcher::SketchObject] Sketch023
  Placement = pos=(-50,0,0) rot=(0.57735,-0.57735,-0.57735;2.0944rad)
  sketch-geometry (11):
    g0: ArcOfCircle CenterX=0 CenterY=18 CenterZ=0 NormalX=0 NormalY=0 NormalZ=1 Radius=5 StartAngle=3.14159 EndAngle=6.28319
    g1: LineSegment StartX=-5 StartY=18 StartZ=0 EndX=-5 EndY=33.5 EndZ=0
    g2: LineSegment StartX=-5 StartY=33.5 StartZ=0 EndX=-10 EndY=33.5 EndZ=0
    g3: LineSegment StartX=-10 StartY=33.5 StartZ=0 EndX=-10 EndY=41.5 EndZ=0
    g4: LineSegment StartX=-10 StartY=41.5 StartZ=0 EndX=10 EndY=41.5 EndZ=0
    g5: LineSegment StartX=10 StartY=41.5 StartZ=0 EndX=10 EndY=33.5 EndZ=0
    g6: LineSegment StartX=10 StartY=33.5 StartZ=0 EndX=5 EndY=33.5 EndZ=0
    g7: LineSegment StartX=5 StartY=33.5 StartZ=0 EndX=5 EndY=18 EndZ=0
    g8: Circle CenterX=-5.5 CenterY=37.5 CenterZ=0 NormalX=0 NormalY=0 NormalZ=1 Radius=1.75
    g9: Circle CenterX=5.5 CenterY=37.5 CenterZ=0 NormalX=0 NormalY=0 NormalZ=1 Radius=1.75
    g10: Circle CenterX=0 CenterY=18 CenterZ=0 NormalX=0 NormalY=0 NormalZ=1 Radius=1.75
  constraints (31):
    c: Tangent(g0,g1) = 1.5708
    c: Coincident(g1,g2)
    c: Horizontal(g2)
    c: Coincident(g2,g3)
    c: Vertical(g3)
    c: Horizontal(g4)
    c: Vertical(g5)
    c: Coincident(g5,g6)
    c: Horizontal(g6)
    c: Coincident(g6,g7)
    c: Coincident(g7,g0)
    c: Vertical(g1)
    c: Vertical(g7)
    c: Radius(g0) = 5
    c: Tangent(g7,g0)
    c: Equal(g1,g7)
    c: Symmetric(g2,g5,g-2)
    c: PointOnObject(g0,g-2)
    c: Distance(g-1,g0) = 18
    c: Distance(g1) = 15.5
    c: Coincident(g10,g0)
    c: Radius(g8) = 1.75
    c: Equal(g8,g9)
    c: Equal(g8,g10)
    c: Symmetric(g9,g8,g-2)
    c: Distance(g9,g8) = 11
    c: DistanceY(g4,g2) = -8
    c: DistanceY(g4,g8) = -4
    c: Distance(g2,g5) = 20
    c: Coincident(g4,g3)
    c: Coincident(g4,g5)
FEATURE [PartDesign::Pad] Pad024
  Length = 40
  Length2 = 100
  Placement = pos=(-50,0,0) rot=(0.57735,-0.57735,-0.57735;2.0944rad)
  Reversed = true
  Sketch = -> Sketch023
  Type = 0
FEATURE [PartDesign::Pad] Pad025
  Length = 70
  Length2 = 100
  Placement = pos=(0,-40,0) rot=(1,0,0;1.5708rad)
  Reversed = true
  Sketch = -> Sketch022
  Type = 0
FEATURE [Part::MultiCommon] Common001
  Shapes = -> [Pad025,Pad024]
FEATURE [Part::Fillet] Fillet011  label="support"
  Base = -> Common001
  Edges = 6 edges r=3: [Edge9,Edge18,Edge39,Edge40,Edge41,Edge42]
FEATURE [App::DocumentObjectGroup] Grupo005  label="parts"
  Group = -> [Cut020,Chamfer005,Pad007,Fusion018,Cut032,Pad023,Fillet011]
FEATURE [Part::FeaturePython] Clone133  label="Clone of support"  # Draft clone (typed FeaturePython)
  Objects = -> [Fillet011]
  Scale = (1,1,1)
FEATURE [Part::FeaturePython] Clone134  label="Clone of support001"  # Draft clone (typed FeaturePython)
  Objects = -> [Fillet011]
  Placement = pos=(0,0,0) rot=(0,0,1;3.14159rad)
  Scale = (1,1,1)
FEATURE [App::DocumentObjectGroup] Grupo003  label="assembly"
  Group = -> [Grupo004,Grupo006,Grupo007,Grupo008,Grupo009,Grupo010,Grupo012,Grupo013,Grupo014,Clone133,Clone134]
FEATURE [Part::FeaturePython] Clone135  label="Clone of support002"  # Draft clone (typed FeaturePython)
  Objects = -> [Fillet011]
  Scale = (1,1,1)
FEATURE [Part::FeaturePython] Clone136  label="Clone of support003"  # Draft clone (typed FeaturePython)
  Objects = -> [Fillet011]
  Placement = pos=(0,0,0) rot=(0,0,1;3.14159rad)
  Scale = (1,1,1)
FEATURE [Sketcher::SketchObject] Sketch024
  Placement = pos=(0,-10,0) rot=(1,0,0;1.5708rad)
  sketch-geometry (4):
    g0: LineSegment StartX=-25.982 StartY=33.9812 StartZ=0 EndX=-30.982 EndY=33.9812 EndZ=0
    g1: LineSegment StartX=-30.982 StartY=33.9812 StartZ=0 EndX=-30.982 EndY=75.7568 EndZ=0
    g2: LineSegment StartX=-30.982 StartY=75.7568 StartZ=0 EndX=-25.982 EndY=77.9812 EndZ=0
    g3: LineSegment StartX=-25.982 StartY=77.9812 StartZ=0 EndX=-25.982 EndY=33.9812 EndZ=0
  constraints (9):
    c: Coincident(g0,g1)
    c: Coincident(g1,g2)
    c: Coincident(g2,g3)
    c: Coincident(g3,g0)
    c: Horizontal(g0)
    c: Vertical(g3)
    c: Distance(g0) = 5
    c: Distance(g3) = 44
    c: Vertical(g1)
FEATURE [PartDesign::Pad] Pad026
  Length = 20
  Length2 = 100
  Placement = pos=(0,-10,0) rot=(1,0,0;1.5708rad)
  Reversed = true
  Sketch = -> Sketch024
  Type = 0
FEATURE [Part::FeaturePython] Clone137  label="Clone of Pad026"  # Draft clone (typed FeaturePython)
  Objects = -> [Pad026]
  Placement = pos=(0,10,0) rot=(0,0.707107,0.707107;3.14159rad)
  Scale = (1,1,1)
FEATURE [Part::Box] Box016  label="Cubo016"
  Height = 4
  Length = 134
  Placement = pos=(-67,-7,47) rot=(0,0,1;0rad)
  Width = 14
FEATURE [Part::Box] Box017  label="Cubo017"
  Height = 4
  Length = 134
  Placement = pos=(7,-67,47) rot=(0,0,1;1.5708rad)
  Width = 14
FEATURE [Part::MultiFuse] Fusion023
  Shapes = -> [Box016,Box017,Pad026,Clone137,Cut034]
FEATURE [Part::Cylinder] Cylinder022  label="Cilindro018"
  Angle = 360
  Height = 80
  Placement = pos=(-40,5.5,37.5) rot=(0,1,0;1.5708rad)
  Radius = 1.75
FEATURE [Part::Cylinder] Cylinder023  label="Cilindro019"
  Angle = 360
  Height = 80
  Placement = pos=(-40,-5.5,37.5) rot=(0,1,0;1.5708rad)
  Radius = 1.75
FEATURE [Part::MultiFuse] Fusion024
  Shapes = -> [Cylinder022,Cylinder023]
FEATURE [Part::Cut] Cut035
  Base = -> Fusion023
  Tool = -> Fusion024
FEATURE [Spreadsheet::Sheet] Spreadsheet  label="configuration"
  cells = A1=COMPONENTS; F1=PRINTER SETTINGS; A3=Servo; B3=Model; C3=TGY-306G-HV; F3=Tolerance; G3=X; H3=0.25; B4=A; C4=31; G4=Y; H4=0.25; B5=B; C5=23; G5=Z; H5=0.25; B6=C; C6=27; G6=default; H6=0.25; B7=D; C7=12; B8=E; C8=32; B9=F; C9=20; A11=Horn; B11=R; B12=r; B13=l; A15=Battery; B15=Model; B16=A; B17=B; B18=C
FEATURE [Part::Cylinder] Cylinder024  label="Cilindro020"
  Angle = 360
  Height = 14
  Placement = pos=(-47,58,7) rot=(1,0,0;1.5708rad)
  Radius = 4.3
FEATURE [Part::MultiFuse] Fusion025
  Shapes = -> [Cylinder024,Pad012]
FEATURE [Part::Cut] Cut036
  Base = -> Cut013
  Tool = -> Fusion025
FEATURE [Part::Feature] Part__Feature154  label="zum_board_basic_pcb"
  Placement = pos=(-24.75,33.5,2) rot=(0,0,-1;1.5708rad)
  shape: bbox 53.36 x 68.6 x 1.91 mm, 540 faces (baked)
FEATURE [Part::Box] Box018  label="Cubo018"
  Height = 10
  Length = 7
  Placement = pos=(-16,28.5,0) rot=(0,0,1;0rad)
  Width = 6
FEATURE [Part::Fillet] Fillet012  label="screw_tunnel001"
  Base = -> Box018
  Edges = 1 edges r=1: [Edge5]
  Placement = pos=(13,-8,0) rot=(0,0,1;3.14159rad)
FEATURE [Sketcher::SketchObject] Sketch025  label="circle"
  sketch-geometry (1):
    g0: Circle CenterX=-9.79521 CenterY=10.1686 CenterZ=0 NormalX=0 NormalY=0 NormalZ=1 Radius=1.85482
FEATURE [PartDesign::Pad] Pad027  label="central_zum_hole"
  Length = 20
  Length2 = 100
  Midplane = true
  Sketch = -> Sketch025
  Type = 0
FEATURE [Sketcher::SketchObject] Sketch026  label="circle001"
  Placement = pos=(20,0,0) rot=(0,0,1;0rad)
  sketch-geometry (1):
    g0: Circle CenterX=-9.79521 CenterY=10.1686 CenterZ=0 NormalX=0 NormalY=0 NormalZ=1 Radius=1.85482
FEATURE [PartDesign::Pad] Pad028  label="central_zum_hole001"
  Length = 20
  Length2 = 100
  Midplane = true
  Placement = pos=(20,0,0) rot=(0,0,1;0rad)
  Sketch = -> Sketch026
  Type = 0
FEATURE [Sketcher::SketchObject] Sketch027  label="circle002"
  Placement = pos=(0,-20,0) rot=(0,0,1;0rad)
  sketch-geometry (1):
    g0: Circle CenterX=-9.79521 CenterY=10.1686 CenterZ=0 NormalX=0 NormalY=0 NormalZ=1 Radius=1.85482
FEATURE [PartDesign::Pad] Pad029  label="central_zum_hole002"
  Length = 20
  Length2 = 100
  Midplane = true
  Placement = pos=(0,-20,0) rot=(0,0,1;0rad)
  Sketch = -> Sketch027
  Type = 0
FEATURE [Sketcher::SketchObject] Sketch028  label="circle003"
  Placement = pos=(20,-20,0) rot=(0,0,1;0rad)
  sketch-geometry (1):
    g0: Circle CenterX=-9.79521 CenterY=10.1686 CenterZ=0 NormalX=0 NormalY=0 NormalZ=1 Radius=1.85482
FEATURE [PartDesign::Pad] Pad030  label="central_zum_hole003"
  Length = 20
  Length2 = 100
  Midplane = true
  Placement = pos=(20,-20,0) rot=(0,0,1;0rad)
  Sketch = -> Sketch028
  Type = 0
FEATURE [Part::MultiFuse] Fusion027  label="central_zum_holes"
  Placement = pos=(-0.25,0,0) rot=(0,0,1;0rad)
  Shapes = -> [Pad030,Pad029,Pad028,Pad027]
FEATURE [Part::Feature] Pad031  label="servo_hole001"
  Placement = pos=(-14,-7.5,-10) rot=(1,0,0;3.14159rad)
  shape: bbox 13 x 30 x 40 mm, 18 faces, 5 solids (baked)
FEATURE [Part::Cut] Cut  label="main_body_basic"
  Base = -> Box001
  Tool = -> Box007
FEATURE [Part::Cut] Cut037  label="main_body_board_bed"
  Base = -> Cut
  Tool = -> Box008
FEATURE [Part::Feature] Pad032  label="servo_hole002"
  Placement = pos=(-14,43,-10) rot=(1,0,0;3.14159rad)
  shape: bbox 13 x 30 x 40 mm, 18 faces, 5 solids (baked)
FEATURE [Part::Feature] Pad033  label="servo_hole003"
  Placement = pos=(60,-7.5,-10) rot=(1,0,0;3.14159rad)
  shape: bbox 13 x 30 x 40 mm, 18 faces, 5 solids (baked)
FEATURE [Part::Feature] Pad034  label="servo_hole004"
  Placement = pos=(60,43,-10) rot=(1,0,0;3.14159rad)
  shape: bbox 13 x 30 x 40 mm, 18 faces, 5 solids (baked)
FEATURE [Part::MultiFuse] Fusion028  label="servo_holes"
  Shapes = -> [Pad031,Pad033,Pad034,Pad032]
FEATURE [Part::Feature] Pad035002  label="central_zum_hole006"
  Placement = pos=(18.6,-41.7,0) rot=(0,0,1;0rad)
  shape: bbox 3.71 x 3.71 x 20 mm, 3 faces (baked)
FEATURE [Part::Feature] Pad035003  label="central_zum_hole007"
  Placement = pos=(-9.3,-41.7,0) rot=(0,0,1;0rad)
  shape: bbox 3.71 x 3.71 x 20 mm, 3 faces (baked)
FEATURE [Part::Feature] Pad035004  label="central_zum_hole008"
  Placement = pos=(33.9,9.15,0) rot=(0,0,1;0rad)
  shape: bbox 3.71 x 3.71 x 20 mm, 3 faces (baked)
FEATURE [Part::MultiFuse] Fusion029  label="arduino_pcb_holes"
  Shapes = -> [Pad035002,Pad035004,Pad035003]
FEATURE [Part::MultiFuse] Fusion030  label="board_holes"
  Placement = pos=(2,-1,0) rot=(0,0,1;0rad)
  Shapes = -> [Fusion027,Fusion029]
FEATURE [Sketcher::SketchObject] Sketch029  label="spacer001"
  Placement = pos=(0,0,5) rot=(0,0,1;0rad)
  sketch-geometry (4):
    g0: LineSegment StartX=-38.4598 StartY=14.9727 StartZ=0 EndX=-35.5033 EndY=14.9727 EndZ=0
    g1: LineSegment StartX=-35.5033 StartY=14.9727 StartZ=0 EndX=-35.5033 EndY=-13.9939 EndZ=0
    g2: LineSegment StartX=-35.5033 StartY=-13.9939 StartZ=0 EndX=-38.4598 EndY=-13.9939 EndZ=0
    g3: LineSegment StartX=-38.4598 StartY=-13.9939 StartZ=0 EndX=-38.4598 EndY=14.9727 EndZ=0
  constraints (8):
    c: Coincident(g0,g1)
    c: Coincident(g1,g2)
    c: Coincident(g2,g3)
    c: Coincident(g3,g0)
    c: Horizontal(g0)
    c: Horizontal(g2)
    c: Vertical(g1)
    c: Vertical(g3)
FEATURE [PartDesign::Pad] Pad035005  label="spacer_left"
  Length = 20
  Length2 = 100
  Midplane = true
  Placement = pos=(0,0,5) rot=(0,0,1;0rad)
  Sketch = -> Sketch029
  Type = 0
FEATURE [Sketcher::SketchObject] Sketch030  label="spacer003"
  Placement = pos=(74,0,5) rot=(0,0,1;0rad)
  sketch-geometry (4):
    g0: LineSegment StartX=-38.4598 StartY=14.9727 StartZ=0 EndX=-35.5033 EndY=14.9727 EndZ=0
    g1: LineSegment StartX=-35.5033 StartY=14.9727 StartZ=0 EndX=-35.5033 EndY=-13.9939 EndZ=0
    g2: LineSegment StartX=-35.5033 StartY=-13.9939 StartZ=0 EndX=-38.4598 EndY=-13.9939 EndZ=0
    g3: LineSegment StartX=-38.4598 StartY=-13.9939 StartZ=0 EndX=-38.4598 EndY=14.9727 EndZ=0
  constraints (8):
    c: Coincident(g0,g1)
    c: Coincident(g1,g2)
    c: Coincident(g2,g3)
    c: Coincident(g3,g0)
    c: Horizontal(g0)
    c: Horizontal(g2)
    c: Vertical(g1)
    c: Vertical(g3)
FEATURE [PartDesign::Pad] Pad035006  label="spacer_right"
  Length = 20
  Length2 = 100
  Midplane = true
  Placement = pos=(74,0,5) rot=(0,0,1;0rad)
  Sketch = -> Sketch030
  Type = 0
FEATURE [Part::MultiFuse] Fusion031  label="servo_spacers"
  Shapes = -> [Pad035005,Pad035006]
FEATURE [Part::Mirroring] Part__Mirroring  label="screw_tunnel (Mirror #26)"
  Base = (0,0,0)
  Normal = (1,0,0)
  Source = -> Fillet006
FEATURE [Part::Mirroring] Part__Mirroring045  label="screw_tunnel001 (Mirror #27)"
  Base = (0,0,0)
  Normal = (1,0,0)
  Source = -> Fillet012
FEATURE [Part::MultiFuse] Fusion032  label="screws_tunnels"
  Shapes = -> [Fillet012,Fillet006,Part__Mirroring,Part__Mirroring045]
FEATURE [Part::Cylinder] Cylinder025  label="Cilindro021"
  Angle = 360
  Height = 30
  Placement = pos=(26,39.75,-10) rot=(0,0,1;0rad)
  Radius = 1.75
FEATURE [Part::Cylinder] Cylinder026  label="Cilindro022"
  Angle = 360
  Height = 30
  Placement = pos=(-26,-38.75,-10) rot=(0,0,1;0rad)
  Radius = 1.75
FEATURE [Part::Cylinder] Cylinder027  label="screw_holes"
  Angle = 360
  Height = 30
  Placement = pos=(26,-38.75,-10) rot=(0,0,1;0rad)
  Radius = 1.75
FEATURE [Part::MultiFuse] Fusion033  label="screw_holes001"
  Shapes = -> [Cylinder,Cylinder025,Cylinder027,Cylinder026]
FEATURE [Part::Cone] Cone001  label="Cono001"
  Angle = 360
  Height = 3
  Placement = pos=(-26,39.75,-4) rot=(0,0,1;0rad)
  Radius1 = 3.8
  Radius2 = 1
FEATURE [Part::Mirroring] Part__Mirroring046  label="Cono (Mirror #25)"
  Base = (0,0,0)
  Normal = (1,0,0)
  Source = -> Cone
FEATURE [Part::Mirroring] Part__Mirroring047  label="Cono001 (Mirror #26)"
  Base = (0,0,0)
  Normal = (1,0,0)
  Source = -> Cone001
FEATURE [Part::MultiFuse] Fusion034  label="cones_holes"
  Shapes = -> [Cone001,Part__Mirroring047,Cone,Part__Mirroring046]
FEATURE [Part::Box] Box019  label="wide_back_hole"
  Height = 16
  Length = 44
  Placement = pos=(-22,36,-2) rot=(0,0,1;0rad)
  Width = 10
FEATURE [Mesh::Feature] Arduino_Uno_R3  label="Arduino Uno R3"
  Placement = pos=(-125.5,-123.5,-10.25) rot=(0,0,-1;1.5708rad)
FEATURE [App::DocumentObjectGroup] Grupo001  label="components"
  Group = -> [Solid001,Fillet,Cut018,Cut031,Grupo011,Part__Feature154,Arduino_Uno_R3]
FEATURE [App::DocumentObjectGroup] Grupo  label="src"
  Group = -> [Grupo001,Grupo005]
FEATURE [Part::Fillet] Fillet013  label="wide_back_hole001"
  Base = -> Box019
  Edges = 4 edges r=2: [Edge2,Edge4,Edge6,Edge8]
FEATURE [Part::Cut] Cut038  label="main_board_holes"
  Base = -> Cut037
  Tool = -> Fusion030
FEATURE [Part::Cut] Cut039  label="main_body_board_servo_holes"
  Base = -> Cut038
  Tool = -> Fusion028
FEATURE [Part::Cut] Cut040  label="main_body_board_spacers"
  Base = -> Cut039
  Tool = -> Fusion031
FEATURE [Part::MultiFuse] Fusion035  label="main_body_board_tunnels"
  Shapes = -> [Cut040,Fusion032]
FEATURE [Part::Cut] Cut041  label="main_body_board_screws_tunnel"
  Base = -> Fusion035
  Tool = -> Fusion033
FEATURE [Part::Cut] Cut042  label="main_body_board_cone_holes"
  Base = -> Cut041
  Tool = -> Fusion034
FEATURE [Part::Cut] Cut043  label="main_body_board_wide_holes"
  Base = -> Cut042
  Tool = -> Fillet013
FEATURE [Part::Cut] Cut044  label="main_boy_board"
  Base = -> Cut043
  Tool = -> Cylinder018
FEATURE [Part::Fillet] Fillet014  label="main_body_board_rounded"
  Base = -> Cut044
  Edges = 4 edges r=1: [Edge1,Edge4,Edge7,Edge68]
  Placement = pos=(0,-0.5,-1) rot=(0,0,1;0rad)
FEATURE [Part::Box] Box020  label="Cubo019"
  Height = 6
  Length = 92
  Placement = pos=(-46,-43,23) rot=(0,0,1;0rad)
  Width = 87
FEATURE [Sketcher::SketchObject] Sketch031
  Placement = pos=(0,0,23) rot=(1,0,0;3.14159rad)
  sketch-geometry (4):
    g0: LineSegment StartX=-44 StartY=41.5 StartZ=0 EndX=44 EndY=41.5 EndZ=0
    g1: LineSegment StartX=44 StartY=41.5 StartZ=0 EndX=44 EndY=-41.5 EndZ=0
    g2: LineSegment StartX=44 StartY=-41.5 StartZ=0 EndX=-44 EndY=-41.5 EndZ=0
    g3: LineSegment StartX=-44 StartY=-41.5 StartZ=0 EndX=-44 EndY=41.5 EndZ=0
  constraints (12):
    c: Coincident(g0,g1)
    c: Coincident(g1,g2)
    c: Coincident(g2,g3)
    c: Coincident(g3,g0)
    c: Horizontal(g0)
    c: Horizontal(g2)
    c: Vertical(g1)
    c: Vertical(g3)
    c: Symmetric(g2,g1,g-2)
    c: Symmetric(g0,g2,g-1)
    c: Distance(g3) = 83
    c: Distance(g2) = 88
FEATURE [PartDesign::Pad] Pad035007
  Length = 2
  Length2 = 100
  Placement = pos=(0,0,23) rot=(1,0,0;3.14159rad)
  Reversed = true
  Sketch = -> Sketch031
  Type = 0
FEATURE [Sketcher::SketchObject] Sketch032
  Placement = pos=(0,0,23) rot=(1,0,0;3.14159rad)
  sketch-geometry (4):
    g0: LineSegment StartX=-29 StartY=36 StartZ=0 EndX=29 EndY=36 EndZ=0
    g1: LineSegment StartX=29 StartY=36 StartZ=0 EndX=29 EndY=-36 EndZ=0
    g2: LineSegment StartX=29 StartY=-36 StartZ=0 EndX=-29 EndY=-36 EndZ=0
    g3: LineSegment StartX=-29 StartY=-36 StartZ=0 EndX=-29 EndY=36 EndZ=0
  constraints (12):
    c: Coincident(g0,g1)
    c: Coincident(g1,g2)
    c: Coincident(g2,g3)
    c: Coincident(g3,g0)
    c: Horizontal(g0)
    c: Horizontal(g2)
    c: Vertical(g1)
    c: Vertical(g3)
    c: Symmetric(g2,g1,g-2)
    c: Symmetric(g0,g2,g-1)
    c: Distance(g3) = 72
    c: Distance(g2) = 58
FEATURE [PartDesign::Pad] Pad035008
  Length = 6
  Length2 = 100
  Placement = pos=(0,0,23) rot=(1,0,0;3.14159rad)
  Reversed = true
  Sketch = -> Sketch032
  Type = 0
FEATURE [Part::MultiFuse] Fusion037  label="down_cover_base"
  Placement = pos=(0,0,-1) rot=(0,0,1;0rad)
  Shapes = -> [Pad035008,Pad035007]
FEATURE [Part::Prism] Prism012  label="Prisma012"
  Circumradius = 3.1
  Height = 10
  Polygon = 6
FEATURE [Sketcher::SketchObject] Sketch033
  Placement = pos=(0,0,40) rot=(0,0,1;0rad)
  sketch-geometry (8):
    g0: LineSegment StartX=-7 StartY=7 StartZ=0 EndX=7 EndY=7 EndZ=0
    g1: LineSegment StartX=8.5 StartY=5.5 StartZ=0 EndX=8.5 EndY=-16.5 EndZ=0
    g2: LineSegment StartX=7 StartY=-18 StartZ=0 EndX=-7 EndY=-18 EndZ=0
    g3: LineSegment StartX=-8.5 StartY=-16.5 StartZ=0 EndX=-8.5 EndY=5.5 EndZ=0
    g4: ArcOfCircle CenterX=-7 CenterY=-16.5 CenterZ=0 NormalX=0 NormalY=0 NormalZ=1 Radius=1.5 StartAngle=3.14159 EndAngle=4.71239
    g5: ArcOfCircle CenterX=-7 CenterY=5.5 CenterZ=0 NormalX=0 NormalY=0 NormalZ=1 Radius=1.5 StartAngle=1.5708 EndAngle=3.14159
    g6: ArcOfCircle CenterX=7 CenterY=5.5 CenterZ=0 NormalX=0 NormalY=0 NormalZ=1 Radius=1.5 StartAngle=0 EndAngle=1.5708
    g7: ArcOfCircle CenterX=7 CenterY=-16.5 CenterZ=0 NormalX=0 NormalY=0 NormalZ=1 Radius=1.5 StartAngle=4.71239 EndAngle=6.28319
  constraints (19):
    c: Horizontal(g0)
    c: Horizontal(g2)
    c: Vertical(g1)
    c: Vertical(g3)
    c: Tangent(g3,g4) = 1.5708
    c: Tangent(g2,g4) = 1.5708
    c: Tangent(g3,g5) = 1.5708
    c: Tangent(g0,g5) = 1.5708
    c: Tangent(g0,g6) = 1.5708
    c: Tangent(g1,g6) = 1.5708
    c: Tangent(g2,g7) = 1.5708
    c: Tangent(g1,g7) = 1.5708
    c: DistanceY(g-1,g0) = 7
    c: DistanceY(g0,g2) = -25
    c: DistanceX(g3,g1) = 17
    c: Symmetric(g3,g1,g-2)
    c: Equal(g0,g2)
    c: Equal(g3,g1)
    c: Radius(g5) = 1.5
FEATURE [PartDesign::Pad] Pad035009  label="hole_cover"
  Length = 35
  Length2 = 100
  Placement = pos=(0,0,40) rot=(0,0,1;0rad)
  Reversed = true
  Sketch = -> Sketch033
  Type = 0
FEATURE [Part::Box] Box021  label="back_cover_hole"
  Height = 10
  Length = 12
  Placement = pos=(-6,30,22) rot=(0,0,1;0rad)
  Width = 16
FEATURE [Part::Box] Box022  label="Cubo021"
  Height = 11
  Length = 6
  Placement = pos=(-28.75,-4.5,14) rot=(0,0,1;0rad)
  Width = 9
FEATURE [Part::Cylinder] Cylinder032  label="Cilindro027"
  Angle = 360
  Height = 68
  Placement = pos=(-34,0,18) rot=(0,1,0;1.5708rad)
  Radius = 1.75
FEATURE [Part::Cut] Cut050
  Base = -> Box022
  Tool = -> Cylinder032
FEATURE [Part::Chamfer] Chamfer020
  Base = -> Cut050
  Edges = 1 edges r=1.5: [Edge3]
FEATURE [Part::Fillet] Fillet015
  Base = -> Chamfer020
  Edges = 2 edges r=1.5: [Edge6,Edge14]
FEATURE [Part::Prism] Prism015  label="Prisma015"
  Circumradius = 3.25
  Height = 10
  Placement = pos=(-17.5,0,18) rot=(-0.250563,-0.935113,0.250563;1.63783rad)
  Polygon = 6
FEATURE [Part::Cut] Cut051
  Base = -> Fillet015
  Tool = -> Prism015
FEATURE [Part::Box] Box023  label="Cubo022"
  Height = 3
  Length = 4
  Placement = pos=(-29.75,-4.5,23) rot=(0,0,1;0rad)
  Width = 9
FEATURE [Part::MultiFuse] Fusion039
  Placement = pos=(-15,-0.5,-1) rot=(0,0,1;0rad)
  Shapes = -> [Cut051,Box023]
FEATURE [Part::Mirroring] Part__Mirroring048  label="Fusion016 (Mirror #31)001"
  Base = (0,0,0)
  Normal = (1,0,0)
  Source = -> Fusion039
FEATURE [Part::Cylinder] Cylinder033  label="up_hole"
  Angle = 360
  Height = 15
  Placement = pos=(-7,26,17) rot=(0,0,1;0rad)
  Radius = 2
FEATURE [Part::Chamfer] Chamfer019  label="up_cover_base"
  Base = -> Box020
  Edges = 8 edges r=1: [Edge1,Edge2,Edge3,Edge5,Edge6,Edge7,Edge10,Edge12]
FEATURE [Part::Cylinder] Cylinder034  label="Cilindro"
  Angle = 360
  Height = 50
  Placement = pos=(0,0,-15) rot=(0,0,1;0rad)
  Radius = 1.75
FEATURE [Part::MultiFuse] Fusion041  label="screw_nut_hole"
  Placement = pos=(37,29.565,9.5) rot=(0,0,1;0rad)
  Shapes = -> [Prism012,Cylinder034]
FEATURE [Part::Mirroring] Part__Mirroring049  label="screw_nut_hole (Mirror #28)"
  Base = (0,0,0)
  Normal = (1,0,0)
  Source = -> Fusion041
FEATURE [Part::Mirroring] Part__Mirroring050  label="screw_nut_hole (Mirror #29)"
  Base = (0,0,0)
  Normal = (0,1,0)
  Source = -> Part__Mirroring049
FEATURE [Part::Mirroring] Part__Mirroring051  label="screw_nut_hole (Mirror #30)"
  Base = (0,0,0)
  Normal = (0,1,0)
  Source = -> Fusion041
FEATURE [Part::MultiFuse] Fusion042  label="screw_nuts_holes"
  Placement = pos=(0,0,7.5) rot=(0,0,1;0rad)
  Shapes = -> [Part__Mirroring051,Fusion041,Part__Mirroring049,Part__Mirroring050]
FEATURE [Part::Cut] Cut052  label="base_cover"
  Base = -> Chamfer019
  Tool = -> Fusion037
FEATURE [Part::Cut] Cut053  label="base_cover_holes"
  Base = -> Cut052
  Tool = -> Fusion042
FEATURE [Part::Cut] Cut054  label="base_cover_up_hole"
  Base = -> Cut053
  Tool = -> Pad035009
FEATURE [Part::MultiFuse] Fusion043
  Shapes = -> [Cylinder033,Box021]
FEATURE [Part::Cut] Cut055  label="base_cover001"
  Base = -> Cut054
  Placement = pos=(0,-0.5,0) rot=(0,0,1;0rad)
  Tool = -> Fusion043
FEATURE [Part::MultiFuse] Fusion044
  Placement = pos=(0,0,1.5) rot=(0,0,1;0rad)
  Shapes = -> [Part__Mirroring048,Fusion039]
FEATURE [Part::MultiFuse] Fusion045  label="cover"
  Placement = pos=(0,0,-1.5) rot=(0,0,1;0rad)
  Shapes = -> [Cut055,Fusion044]
